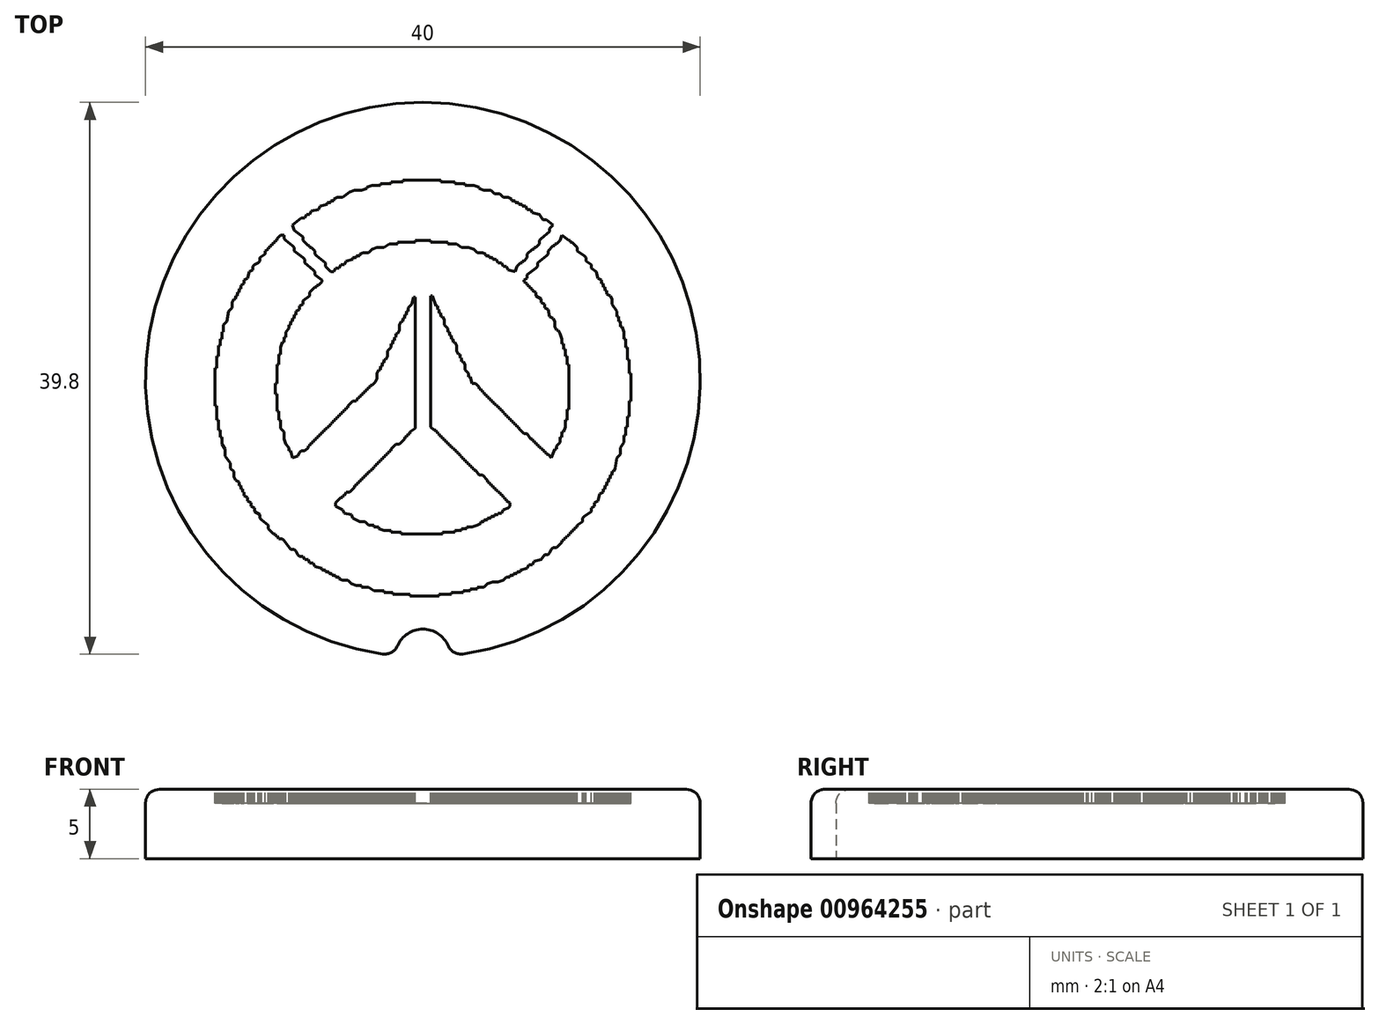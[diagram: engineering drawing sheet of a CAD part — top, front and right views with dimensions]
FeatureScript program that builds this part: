
annotation { "Feature Type Name" : "Feature", "Feature Type Description" : "" }
export const myFeature = defineFeature(function(context is Context, id is Id, definition is map)
    precondition{}
    {
        {
            var Q0;
            Q0=qCreatedBy(makeId("Front.planeOp"),FACE);
            var sketch = newSketch(context, id + "F0", { "sketchPlane" : qUnion([Q0])});
            skLineSegment(sketch, "E0.bottom", {"start": v(0, 0) * mm, "end": v(-20, 0) * mm});
            skLineSegment(sketch, "E0.top", {"start": v(0, 5) * mm, "end": v(-20, 5) * mm});
            skLineSegment(sketch, "E0.left", {"start": v(0, 0) * mm, "end": v(0, 5) * mm});
            skLineSegment(sketch, "E0.right", {"start": v(-20, 0) * mm, "end": v(-20, 5) * mm});
            skSolve(sketch);
        }
        {
            var Q0;
            Q0 = qSketchRegion(id + "F0", true);
            var Q1;
            Q1=sQuery(id+"F0.wireOp",EDGE,"E0.left");
            revolve(context, id + "F1", {"surfaceOperationType" : NewSurfaceOperationType.NEW, "entities" : qUnion([Q0]), "axis" : qUnion([Q1]), "revolveType" : RevolveType.FULL});
        }
        {
            var Q0;
            Q0=qCreatedBy(makeId("Top.planeOp"),FACE);
            var sketch = newSketch(context, id + "F2", { "sketchPlane" : qUnion([Q0])});
            skLineSegment(sketch, "E1", {"start": v(0, 0) * mm, "end": v(0, -20) * mm});
            skCircle(sketch, "E2", {"center": v(0, -20) * mm, "radius": 2 * mm});
            skSolve(sketch);
        }
        {
            var Q0;
            Q0 = qSketchRegion(id + "F2", true);
            extrude(context, id + "F3", {"entities" : qUnion([Q0]), "operationType" : NewBodyOperationType.REMOVE, "depth" : 25 * mm, "offsetDistance" : 25 * mm});
        }
        {
            var Q0;
            Q0=makeQuery(id+"F1.opRevolve","SWEPT_EDGE",EDGE,{"disambiguationData":[OSD([sQuery(id+"F0.wireOp",EDGE,"E0.top"),sQuery(id+"F0.wireOp",EDGE,"E0.right")])]});
            fillet(context, id + "F4", {"entities" : qUnion([Q0]), "radius" : 1 * mm, "tangentPropagation" : true, "allowEdgeOverflow" : false});
        }
        {
            var Q0;
            Q0=makeQuery(id+"F3.boolean.opBoolean","INTERSECT",EDGE,{"derivedFrom":[makeQuery(id+"F1.opRevolve","SWEPT_FACE",FACE,{"disambiguationData":[OSD([sQuery(id+"F0.wireOp",EDGE,"E0.top")])]}),makeQuery(id+"F3.opExtrude","SWEPT_FACE",FACE,{"disambiguationData":[OSD([sQuery(id+"F2.wireOp",EDGE,"E2")])]})]});
            fillet(context, id + "F5", {"entities" : qUnion([Q0]), "radius" : 1 * mm, "tangentPropagation" : true, "allowEdgeOverflow" : false});
        }
        {
            var Q0;
            Q0=qCreatedBy(makeId("Top.planeOp"),FACE);
            cPlane(context, id + "F6", {"entities" : qUnion([Q0]), "cplaneType" : CPlaneType.OFFSET, "offset" : 5 * mm, "width" : 150 * mm, "height" : 150 * mm});
        }
        {
            var Q0;
            Q0=qCreatedBy(id+"F6.planeOp",FACE);
            var sketch = newSketch(context, id + "F7", { "sketchPlane" : qUnion([Q0])});
            skLineSegment(sketch, "E3", {"start": v(-1.43, 14.4) * mm, "end": v(-1.43, 14.28) * mm});
            skLineSegment(sketch, "E4", {"start": v(-1.43, 14.28) * mm, "end": v(-2.3, 14.28) * mm});
            skLineSegment(sketch, "E5", {"start": v(-2.3, 14.28) * mm, "end": v(-2.3, 14.15) * mm});
            skLineSegment(sketch, "E6", {"start": v(-2.3, 14.15) * mm, "end": v(-3.05, 14.15) * mm});
            skLineSegment(sketch, "E7", {"start": v(-3.05, 14.15) * mm, "end": v(-3.05, 14.03) * mm});
            skLineSegment(sketch, "E8", {"start": v(-3.05, 14.03) * mm, "end": v(-3.67, 14.03) * mm});
            skLineSegment(sketch, "E9", {"start": v(-3.67, 14.03) * mm, "end": v(-4.05, 13.9) * mm});
            skLineSegment(sketch, "E10", {"start": v(-4.05, 13.9) * mm, "end": v(-4.05, 13.78) * mm});
            skLineSegment(sketch, "E11", {"start": v(-4.05, 13.78) * mm, "end": v(-4.42, 13.65) * mm});
            skLineSegment(sketch, "E12", {"start": v(-4.42, 13.65) * mm, "end": v(-4.92, 13.65) * mm});
            skLineSegment(sketch, "E13", {"start": v(-4.92, 13.65) * mm, "end": v(-5.3, 13.53) * mm});
            skLineSegment(sketch, "E14", {"start": v(-5.3, 13.53) * mm, "end": v(-5.79, 13.16) * mm});
            skLineSegment(sketch, "E15", {"start": v(-5.79, 13.16) * mm, "end": v(-6.16, 13.16) * mm});
            skLineSegment(sketch, "E16", {"start": v(-6.16, 13.16) * mm, "end": v(-6.41, 13.03) * mm});
            skLineSegment(sketch, "E17", {"start": v(-6.41, 13.03) * mm, "end": v(-6.41, 12.9) * mm});
            skLineSegment(sketch, "E18", {"start": v(-6.41, 12.9) * mm, "end": v(-6.66, 12.9) * mm});
            skLineSegment(sketch, "E19", {"start": v(-6.66, 12.9) * mm, "end": v(-6.66, 12.78) * mm});
            skLineSegment(sketch, "E20", {"start": v(-6.66, 12.78) * mm, "end": v(-6.9, 12.78) * mm});
            skLineSegment(sketch, "E21", {"start": v(-6.9, 12.78) * mm, "end": v(-6.9, 12.66) * mm});
            skLineSegment(sketch, "E22", {"start": v(-6.9, 12.66) * mm, "end": v(-7.4, 12.53) * mm});
            skLineSegment(sketch, "E23", {"start": v(-7.4, 12.53) * mm, "end": v(-7.53, 12.28) * mm});
            skLineSegment(sketch, "E24", {"start": v(-7.53, 12.28) * mm, "end": v(-8.03, 12.16) * mm});
            skLineSegment(sketch, "E25", {"start": v(-8.03, 12.16) * mm, "end": v(-8.15, 11.91) * mm});
            skLineSegment(sketch, "E26", {"start": v(-8.15, 11.91) * mm, "end": v(-8.4, 11.91) * mm});
            skLineSegment(sketch, "E27", {"start": v(-8.4, 11.91) * mm, "end": v(-8.53, 11.66) * mm});
            skLineSegment(sketch, "E28", {"start": v(-8.53, 11.66) * mm, "end": v(-8.78, 11.66) * mm});
            skLineSegment(sketch, "E29", {"start": v(-8.78, 11.66) * mm, "end": v(-9.4, 11.16) * mm});
            skLineSegment(sketch, "E30", {"start": v(-9.4, 11.16) * mm, "end": v(-9.27, 10.8) * mm});
            skLineSegment(sketch, "E31", {"start": v(-9.27, 10.8) * mm, "end": v(-8.65, 10.3) * mm});
            skLineSegment(sketch, "E32", {"start": v(-8.65, 10.3) * mm, "end": v(-8.65, 10.04) * mm});
            skLineSegment(sketch, "E33", {"start": v(-8.65, 10.04) * mm, "end": v(-8.53, 9.92) * mm});
            skLineSegment(sketch, "E34", {"start": v(-8.53, 9.92) * mm, "end": v(-8.28, 9.67) * mm});
            skLineSegment(sketch, "E35", {"start": v(-8.28, 9.67) * mm, "end": v(-8.15, 9.67) * mm});
            skLineSegment(sketch, "E36", {"start": v(-8.15, 9.67) * mm, "end": v(-8.15, 9.55) * mm});
            skLineSegment(sketch, "E37", {"start": v(-8.15, 9.55) * mm, "end": v(-8.03, 9.55) * mm});
            skLineSegment(sketch, "E38", {"start": v(-8.03, 9.55) * mm, "end": v(-7.78, 9.3) * mm});
            skLineSegment(sketch, "E39", {"start": v(-7.78, 9.3) * mm, "end": v(-7.78, 9.05) * mm});
            skLineSegment(sketch, "E40", {"start": v(-7.78, 9.05) * mm, "end": v(-7.66, 8.92) * mm});
            skLineSegment(sketch, "E41", {"start": v(-7.66, 8.92) * mm, "end": v(-7.03, 8.42) * mm});
            skLineSegment(sketch, "E42", {"start": v(-7.03, 8.42) * mm, "end": v(-7.03, 8.18) * mm});
            skLineSegment(sketch, "E43", {"start": v(-7.03, 8.18) * mm, "end": v(-6.9, 8.05) * mm});
            skLineSegment(sketch, "E44", {"start": v(-6.9, 8.05) * mm, "end": v(-6.78, 7.93) * mm});
            skLineSegment(sketch, "E45", {"start": v(-6.78, 7.93) * mm, "end": v(-6.66, 7.8) * mm});
            skLineSegment(sketch, "E46", {"start": v(-6.66, 7.8) * mm, "end": v(-6.41, 7.8) * mm});
            skLineSegment(sketch, "E47", {"start": v(-6.41, 7.8) * mm, "end": v(-6.29, 8.05) * mm});
            skLineSegment(sketch, "E48", {"start": v(-6.29, 8.05) * mm, "end": v(-6.04, 8.05) * mm});
            skLineSegment(sketch, "E49", {"start": v(-6.04, 8.05) * mm, "end": v(-5.91, 8.3) * mm});
            skLineSegment(sketch, "E50", {"start": v(-5.91, 8.3) * mm, "end": v(-5.66, 8.3) * mm});
            skLineSegment(sketch, "E51", {"start": v(-5.66, 8.3) * mm, "end": v(-5.54, 8.55) * mm});
            skLineSegment(sketch, "E52", {"start": v(-5.54, 8.55) * mm, "end": v(-5.04, 8.67) * mm});
            skLineSegment(sketch, "E53", {"start": v(-5.04, 8.67) * mm, "end": v(-5.04, 8.8) * mm});
            skLineSegment(sketch, "E54", {"start": v(-5.04, 8.8) * mm, "end": v(-4.8, 8.8) * mm});
            skLineSegment(sketch, "E55", {"start": v(-4.8, 8.8) * mm, "end": v(-4.8, 8.92) * mm});
            skLineSegment(sketch, "E56", {"start": v(-4.8, 8.92) * mm, "end": v(-4.54, 8.92) * mm});
            skLineSegment(sketch, "E57", {"start": v(-4.54, 8.92) * mm, "end": v(-4.54, 9.05) * mm});
            skLineSegment(sketch, "E58", {"start": v(-4.54, 9.05) * mm, "end": v(-4.3, 9.17) * mm});
            skLineSegment(sketch, "E59", {"start": v(-4.3, 9.17) * mm, "end": v(-3.92, 9.17) * mm});
            skLineSegment(sketch, "E60", {"start": v(-3.92, 9.17) * mm, "end": v(-3.67, 9.42) * mm});
            skLineSegment(sketch, "E61", {"start": v(-3.67, 9.42) * mm, "end": v(-3.3, 9.55) * mm});
            skLineSegment(sketch, "E62", {"start": v(-3.3, 9.55) * mm, "end": v(-2.8, 9.55) * mm});
            skLineSegment(sketch, "E63", {"start": v(-2.8, 9.55) * mm, "end": v(-2.43, 9.8) * mm});
            skLineSegment(sketch, "E64", {"start": v(-2.43, 9.8) * mm, "end": v(-1.8, 9.8) * mm});
            skLineSegment(sketch, "E65", {"start": v(-1.8, 9.8) * mm, "end": v(-1.8, 9.92) * mm});
            skLineSegment(sketch, "E66", {"start": v(-1.8, 9.92) * mm, "end": v(-1.43, 9.92) * mm});
            skLineSegment(sketch, "E67", {"start": v(-1.43, 9.92) * mm, "end": v(-0.56, 9.92) * mm});
            skLineSegment(sketch, "E68", {"start": v(-0.56, 9.92) * mm, "end": v(-0.56, 10.04) * mm});
            skLineSegment(sketch, "E69", {"start": v(-0.56, 10.04) * mm, "end": v(-0.19, 10.04) * mm});
            skLineSegment(sketch, "E70", {"start": v(-0.19, 10.04) * mm, "end": v(0.19, 10.04) * mm});
            skLineSegment(sketch, "E71", {"start": v(0.19, 10.04) * mm, "end": v(0.56, 10.04) * mm});
            skLineSegment(sketch, "E72", {"start": v(0.56, 10.04) * mm, "end": v(0.56, 9.92) * mm});
            skLineSegment(sketch, "E73", {"start": v(0.56, 9.92) * mm, "end": v(0.93, 9.92) * mm});
            skLineSegment(sketch, "E74", {"start": v(0.93, 9.92) * mm, "end": v(1.8, 9.92) * mm});
            skLineSegment(sketch, "E75", {"start": v(1.8, 9.92) * mm, "end": v(1.8, 9.8) * mm});
            skLineSegment(sketch, "E76", {"start": v(1.8, 9.8) * mm, "end": v(2.43, 9.8) * mm});
            skLineSegment(sketch, "E77", {"start": v(2.43, 9.8) * mm, "end": v(2.8, 9.55) * mm});
            skLineSegment(sketch, "E78", {"start": v(2.8, 9.55) * mm, "end": v(3.3, 9.55) * mm});
            skLineSegment(sketch, "E79", {"start": v(3.3, 9.55) * mm, "end": v(3.67, 9.42) * mm});
            skLineSegment(sketch, "E80", {"start": v(3.67, 9.42) * mm, "end": v(3.92, 9.17) * mm});
            skLineSegment(sketch, "E81", {"start": v(3.92, 9.17) * mm, "end": v(4.3, 9.17) * mm});
            skLineSegment(sketch, "E82", {"start": v(4.3, 9.17) * mm, "end": v(4.54, 9.05) * mm});
            skLineSegment(sketch, "E83", {"start": v(4.54, 9.05) * mm, "end": v(4.54, 8.92) * mm});
            skLineSegment(sketch, "E84", {"start": v(4.54, 8.92) * mm, "end": v(4.8, 8.92) * mm});
            skLineSegment(sketch, "E85", {"start": v(4.8, 8.92) * mm, "end": v(4.8, 8.8) * mm});
            skLineSegment(sketch, "E86", {"start": v(4.8, 8.8) * mm, "end": v(5.04, 8.8) * mm});
            skLineSegment(sketch, "E87", {"start": v(5.04, 8.8) * mm, "end": v(5.04, 8.67) * mm});
            skLineSegment(sketch, "E88", {"start": v(5.04, 8.67) * mm, "end": v(5.3, 8.67) * mm});
            skLineSegment(sketch, "E89", {"start": v(5.3, 8.67) * mm, "end": v(5.41, 8.42) * mm});
            skLineSegment(sketch, "E90", {"start": v(5.41, 8.42) * mm, "end": v(5.66, 8.42) * mm});
            skLineSegment(sketch, "E91", {"start": v(5.66, 8.42) * mm, "end": v(5.79, 8.18) * mm});
            skLineSegment(sketch, "E92", {"start": v(5.79, 8.18) * mm, "end": v(6.04, 8.18) * mm});
            skLineSegment(sketch, "E93", {"start": v(6.04, 8.18) * mm, "end": v(6.16, 7.93) * mm});
            skLineSegment(sketch, "E94", {"start": v(6.16, 7.93) * mm, "end": v(6.66, 7.8) * mm});
            skLineSegment(sketch, "E95", {"start": v(6.66, 7.8) * mm, "end": v(6.78, 8.18) * mm});
            skLineSegment(sketch, "E96", {"start": v(6.78, 8.18) * mm, "end": v(7.03, 8.42) * mm});
            skLineSegment(sketch, "E97", {"start": v(7.03, 8.42) * mm, "end": v(7.16, 8.42) * mm});
            skLineSegment(sketch, "E98", {"start": v(7.16, 8.42) * mm, "end": v(7.16, 8.55) * mm});
            skLineSegment(sketch, "E99", {"start": v(7.16, 8.55) * mm, "end": v(7.28, 8.55) * mm});
            skLineSegment(sketch, "E100", {"start": v(7.28, 8.55) * mm, "end": v(7.53, 8.8) * mm});
            skLineSegment(sketch, "E101", {"start": v(7.53, 8.8) * mm, "end": v(7.53, 9.05) * mm});
            skLineSegment(sketch, "E102", {"start": v(7.53, 9.05) * mm, "end": v(7.66, 9.17) * mm});
            skLineSegment(sketch, "E103", {"start": v(7.66, 9.17) * mm, "end": v(7.9, 9.42) * mm});
            skLineSegment(sketch, "E104", {"start": v(7.9, 9.42) * mm, "end": v(8.03, 9.42) * mm});
            skLineSegment(sketch, "E105", {"start": v(8.03, 9.42) * mm, "end": v(8.03, 9.55) * mm});
            skLineSegment(sketch, "E106", {"start": v(8.03, 9.55) * mm, "end": v(8.15, 9.55) * mm});
            skLineSegment(sketch, "E107", {"start": v(8.15, 9.55) * mm, "end": v(8.4, 9.8) * mm});
            skLineSegment(sketch, "E108", {"start": v(8.4, 9.8) * mm, "end": v(8.4, 10.04) * mm});
            skLineSegment(sketch, "E109", {"start": v(8.4, 10.04) * mm, "end": v(8.53, 10.17) * mm});
            skLineSegment(sketch, "E110", {"start": v(8.53, 10.17) * mm, "end": v(9.15, 10.67) * mm});
            skLineSegment(sketch, "E111", {"start": v(9.15, 10.67) * mm, "end": v(9.15, 10.91) * mm});
            skLineSegment(sketch, "E112", {"start": v(9.15, 10.91) * mm, "end": v(9.4, 11.16) * mm});
            skLineSegment(sketch, "E113", {"start": v(9.4, 11.16) * mm, "end": v(8.9, 11.54) * mm});
            skLineSegment(sketch, "E114", {"start": v(8.9, 11.54) * mm, "end": v(8.65, 11.54) * mm});
            skLineSegment(sketch, "E115", {"start": v(8.65, 11.54) * mm, "end": v(8.4, 11.91) * mm});
            skLineSegment(sketch, "E116", {"start": v(8.4, 11.91) * mm, "end": v(7.9, 12.03) * mm});
            skLineSegment(sketch, "E117", {"start": v(7.9, 12.03) * mm, "end": v(7.78, 12.28) * mm});
            skLineSegment(sketch, "E118", {"start": v(7.78, 12.28) * mm, "end": v(7.53, 12.28) * mm});
            skLineSegment(sketch, "E119", {"start": v(7.53, 12.28) * mm, "end": v(7.4, 12.53) * mm});
            skLineSegment(sketch, "E120", {"start": v(7.4, 12.53) * mm, "end": v(7.16, 12.53) * mm});
            skLineSegment(sketch, "E121", {"start": v(7.16, 12.53) * mm, "end": v(7.16, 12.66) * mm});
            skLineSegment(sketch, "E122", {"start": v(7.16, 12.66) * mm, "end": v(6.9, 12.66) * mm});
            skLineSegment(sketch, "E123", {"start": v(6.9, 12.66) * mm, "end": v(6.9, 12.78) * mm});
            skLineSegment(sketch, "E124", {"start": v(6.9, 12.78) * mm, "end": v(6.66, 12.78) * mm});
            skLineSegment(sketch, "E125", {"start": v(6.66, 12.78) * mm, "end": v(6.66, 12.9) * mm});
            skLineSegment(sketch, "E126", {"start": v(6.66, 12.9) * mm, "end": v(6.41, 12.9) * mm});
            skLineSegment(sketch, "E127", {"start": v(6.41, 12.9) * mm, "end": v(6.41, 13.03) * mm});
            skLineSegment(sketch, "E128", {"start": v(6.41, 13.03) * mm, "end": v(6.16, 13.16) * mm});
            skLineSegment(sketch, "E129", {"start": v(6.16, 13.16) * mm, "end": v(5.79, 13.16) * mm});
            skLineSegment(sketch, "E130", {"start": v(5.79, 13.16) * mm, "end": v(5.54, 13.4) * mm});
            skLineSegment(sketch, "E131", {"start": v(5.54, 13.4) * mm, "end": v(5.17, 13.4) * mm});
            skLineSegment(sketch, "E132", {"start": v(5.17, 13.4) * mm, "end": v(4.92, 13.65) * mm});
            skLineSegment(sketch, "E133", {"start": v(4.92, 13.65) * mm, "end": v(4.42, 13.65) * mm});
            skLineSegment(sketch, "E134", {"start": v(4.42, 13.65) * mm, "end": v(4.05, 13.78) * mm});
            skLineSegment(sketch, "E135", {"start": v(4.05, 13.78) * mm, "end": v(4.05, 13.9) * mm});
            skLineSegment(sketch, "E136", {"start": v(4.05, 13.9) * mm, "end": v(3.67, 14.03) * mm});
            skLineSegment(sketch, "E137", {"start": v(3.67, 14.03) * mm, "end": v(3.05, 14.03) * mm});
            skLineSegment(sketch, "E138", {"start": v(3.05, 14.03) * mm, "end": v(3.05, 14.15) * mm});
            skLineSegment(sketch, "E139", {"start": v(3.05, 14.15) * mm, "end": v(2.3, 14.15) * mm});
            skLineSegment(sketch, "E140", {"start": v(2.3, 14.15) * mm, "end": v(2.3, 14.28) * mm});
            skLineSegment(sketch, "E141", {"start": v(2.3, 14.28) * mm, "end": v(1.3, 14.28) * mm});
            skLineSegment(sketch, "E142", {"start": v(1.3, 14.28) * mm, "end": v(1.3, 14.4) * mm});
            skLineSegment(sketch, "E143", {"start": v(1.3, 14.4) * mm, "end": v(0.93, 14.4) * mm});
            skLineSegment(sketch, "E144", {"start": v(0.93, 14.4) * mm, "end": v(0.44, 14.4) * mm});
            skLineSegment(sketch, "E145", {"start": v(0.44, 14.4) * mm, "end": v(0.31, 14.4) * mm});
            skLineSegment(sketch, "E146", {"start": v(0.31, 14.4) * mm, "end": v(0.19, 14.4) * mm});
            skLineSegment(sketch, "E147", {"start": v(0.19, 14.4) * mm, "end": v(0.06, 14.4) * mm});
            skLineSegment(sketch, "E148", {"start": v(0.06, 14.4) * mm, "end": v(-0.06, 14.4) * mm});
            skLineSegment(sketch, "E149", {"start": v(-0.06, 14.4) * mm, "end": v(-0.19, 14.4) * mm});
            skLineSegment(sketch, "E150", {"start": v(-0.19, 14.4) * mm, "end": v(-0.31, 14.4) * mm});
            skLineSegment(sketch, "E151", {"start": v(-0.31, 14.4) * mm, "end": v(-0.44, 14.4) * mm});
            skLineSegment(sketch, "E152", {"start": v(-0.44, 14.4) * mm, "end": v(-0.56, 14.4) * mm});
            skLineSegment(sketch, "E153", {"start": v(-0.56, 14.4) * mm, "end": v(-0.68, 14.4) * mm});
            skLineSegment(sketch, "E154", {"start": v(-0.68, 14.4) * mm, "end": v(-0.8, 14.4) * mm});
            skLineSegment(sketch, "E155", {"start": v(-0.8, 14.4) * mm, "end": v(-0.93, 14.4) * mm});
            skLineSegment(sketch, "E156", {"start": v(-0.93, 14.4) * mm, "end": v(-1.43, 14.4) * mm});
            skLineSegment(sketch, "E157", {"start": v(-10.27, 10.42) * mm, "end": v(-10.52, 10.17) * mm});
            skLineSegment(sketch, "E158", {"start": v(-10.52, 10.17) * mm, "end": v(-10.52, 10.04) * mm});
            skLineSegment(sketch, "E159", {"start": v(-10.52, 10.04) * mm, "end": v(-10.64, 10.04) * mm});
            skLineSegment(sketch, "E160", {"start": v(-10.64, 10.04) * mm, "end": v(-10.64, 9.92) * mm});
            skLineSegment(sketch, "E161", {"start": v(-10.64, 9.92) * mm, "end": v(-10.77, 9.92) * mm});
            skLineSegment(sketch, "E162", {"start": v(-10.77, 9.92) * mm, "end": v(-10.77, 9.8) * mm});
            skLineSegment(sketch, "E163", {"start": v(-10.77, 9.8) * mm, "end": v(-10.9, 9.8) * mm});
            skLineSegment(sketch, "E164", {"start": v(-10.9, 9.8) * mm, "end": v(-10.9, 9.67) * mm});
            skLineSegment(sketch, "E165", {"start": v(-10.9, 9.67) * mm, "end": v(-11.02, 9.67) * mm});
            skLineSegment(sketch, "E166", {"start": v(-11.02, 9.67) * mm, "end": v(-11.02, 9.55) * mm});
            skLineSegment(sketch, "E167", {"start": v(-11.02, 9.55) * mm, "end": v(-11.14, 9.55) * mm});
            skLineSegment(sketch, "E168", {"start": v(-11.14, 9.55) * mm, "end": v(-11.14, 9.42) * mm});
            skLineSegment(sketch, "E169", {"start": v(-11.14, 9.42) * mm, "end": v(-11.4, 9.3) * mm});
            skLineSegment(sketch, "E170", {"start": v(-11.4, 9.3) * mm, "end": v(-11.4, 9.05) * mm});
            skLineSegment(sketch, "E171", {"start": v(-11.4, 9.05) * mm, "end": v(-11.76, 8.8) * mm});
            skLineSegment(sketch, "E172", {"start": v(-11.76, 8.8) * mm, "end": v(-11.76, 8.55) * mm});
            skLineSegment(sketch, "E173", {"start": v(-11.76, 8.55) * mm, "end": v(-11.89, 8.42) * mm});
            skLineSegment(sketch, "E174", {"start": v(-11.89, 8.42) * mm, "end": v(-12.14, 8.3) * mm});
            skLineSegment(sketch, "E175", {"start": v(-12.14, 8.3) * mm, "end": v(-12.26, 8.18) * mm});
            skLineSegment(sketch, "E176", {"start": v(-12.26, 8.18) * mm, "end": v(-12.26, 7.93) * mm});
            skLineSegment(sketch, "E177", {"start": v(-12.26, 7.93) * mm, "end": v(-12.51, 7.8) * mm});
            skLineSegment(sketch, "E178", {"start": v(-12.51, 7.8) * mm, "end": v(-12.63, 7.3) * mm});
            skLineSegment(sketch, "E179", {"start": v(-12.63, 7.3) * mm, "end": v(-12.88, 7.18) * mm});
            skLineSegment(sketch, "E180", {"start": v(-12.88, 7.18) * mm, "end": v(-12.88, 6.93) * mm});
            skLineSegment(sketch, "E181", {"start": v(-12.88, 6.93) * mm, "end": v(-13.13, 6.8) * mm});
            skLineSegment(sketch, "E182", {"start": v(-13.13, 6.8) * mm, "end": v(-13.13, 6.56) * mm});
            skLineSegment(sketch, "E183", {"start": v(-13.13, 6.56) * mm, "end": v(-13.26, 6.56) * mm});
            skLineSegment(sketch, "E184", {"start": v(-13.26, 6.56) * mm, "end": v(-13.26, 6.3) * mm});
            skLineSegment(sketch, "E185", {"start": v(-13.26, 6.3) * mm, "end": v(-13.38, 6.3) * mm});
            skLineSegment(sketch, "E186", {"start": v(-13.38, 6.3) * mm, "end": v(-13.38, 6.06) * mm});
            skLineSegment(sketch, "E187", {"start": v(-13.38, 6.06) * mm, "end": v(-13.5, 6.06) * mm});
            skLineSegment(sketch, "E188", {"start": v(-13.5, 6.06) * mm, "end": v(-13.5, 5.81) * mm});
            skLineSegment(sketch, "E189", {"start": v(-13.5, 5.81) * mm, "end": v(-13.63, 5.81) * mm});
            skLineSegment(sketch, "E190", {"start": v(-13.63, 5.81) * mm, "end": v(-13.76, 5.56) * mm});
            skLineSegment(sketch, "E191", {"start": v(-13.76, 5.56) * mm, "end": v(-13.76, 5.19) * mm});
            skLineSegment(sketch, "E192", {"start": v(-13.76, 5.19) * mm, "end": v(-14, 4.94) * mm});
            skLineSegment(sketch, "E193", {"start": v(-14, 4.94) * mm, "end": v(-14.13, 4.2) * mm});
            skLineSegment(sketch, "E194", {"start": v(-14.13, 4.2) * mm, "end": v(-14.38, 3.94) * mm});
            skLineSegment(sketch, "E195", {"start": v(-14.38, 3.94) * mm, "end": v(-14.38, 3.45) * mm});
            skLineSegment(sketch, "E196", {"start": v(-14.38, 3.45) * mm, "end": v(-14.5, 3.45) * mm});
            skLineSegment(sketch, "E197", {"start": v(-14.5, 3.45) * mm, "end": v(-14.5, 2.95) * mm});
            skLineSegment(sketch, "E198", {"start": v(-14.5, 2.95) * mm, "end": v(-14.63, 2.95) * mm});
            skLineSegment(sketch, "E199", {"start": v(-14.63, 2.95) * mm, "end": v(-14.63, 2.45) * mm});
            skLineSegment(sketch, "E200", {"start": v(-14.63, 2.45) * mm, "end": v(-14.75, 2.45) * mm});
            skLineSegment(sketch, "E201", {"start": v(-14.75, 2.45) * mm, "end": v(-14.75, 1.7) * mm});
            skLineSegment(sketch, "E202", {"start": v(-14.75, 1.7) * mm, "end": v(-14.88, 1.7) * mm});
            skLineSegment(sketch, "E203", {"start": v(-14.88, 1.7) * mm, "end": v(-14.88, 0.83) * mm});
            skLineSegment(sketch, "E204", {"start": v(-14.88, 0.83) * mm, "end": v(-15, 0.83) * mm});
            skLineSegment(sketch, "E205", {"start": v(-15, 0.83) * mm, "end": v(-15, 0.46) * mm});
            skLineSegment(sketch, "E206", {"start": v(-15, 0.46) * mm, "end": v(-15, -0.04) * mm});
            skLineSegment(sketch, "E207", {"start": v(-15, -0.04) * mm, "end": v(-15, -0.16) * mm});
            skLineSegment(sketch, "E208", {"start": v(-15, -0.16) * mm, "end": v(-15, -0.29) * mm});
            skLineSegment(sketch, "E209", {"start": v(-15, -0.29) * mm, "end": v(-15, -0.41) * mm});
            skLineSegment(sketch, "E210", {"start": v(-15, -0.41) * mm, "end": v(-15, -0.54) * mm});
            skLineSegment(sketch, "E211", {"start": v(-15, -0.54) * mm, "end": v(-15, -0.66) * mm});
            skLineSegment(sketch, "E212", {"start": v(-15, -0.66) * mm, "end": v(-15, -0.79) * mm});
            skLineSegment(sketch, "E213", {"start": v(-15, -0.79) * mm, "end": v(-15, -0.91) * mm});
            skLineSegment(sketch, "E214", {"start": v(-15, -0.91) * mm, "end": v(-15, -1.04) * mm});
            skLineSegment(sketch, "E215", {"start": v(-15, -1.04) * mm, "end": v(-15, -1.16) * mm});
            skLineSegment(sketch, "E216", {"start": v(-15, -1.16) * mm, "end": v(-15, -1.28) * mm});
            skLineSegment(sketch, "E217", {"start": v(-15, -1.28) * mm, "end": v(-15, -1.4) * mm});
            skLineSegment(sketch, "E218", {"start": v(-15, -1.4) * mm, "end": v(-15, -1.9) * mm});
            skLineSegment(sketch, "E219", {"start": v(-15, -1.9) * mm, "end": v(-14.88, -1.9) * mm});
            skLineSegment(sketch, "E220", {"start": v(-14.88, -1.9) * mm, "end": v(-14.88, -2.9) * mm});
            skLineSegment(sketch, "E221", {"start": v(-14.88, -2.9) * mm, "end": v(-14.75, -2.9) * mm});
            skLineSegment(sketch, "E222", {"start": v(-14.75, -2.9) * mm, "end": v(-14.75, -3.65) * mm});
            skLineSegment(sketch, "E223", {"start": v(-14.75, -3.65) * mm, "end": v(-14.63, -3.65) * mm});
            skLineSegment(sketch, "E224", {"start": v(-14.63, -3.65) * mm, "end": v(-14.63, -4.15) * mm});
            skLineSegment(sketch, "E225", {"start": v(-14.63, -4.15) * mm, "end": v(-14.5, -4.15) * mm});
            skLineSegment(sketch, "E226", {"start": v(-14.5, -4.15) * mm, "end": v(-14.5, -4.65) * mm});
            skLineSegment(sketch, "E227", {"start": v(-14.5, -4.65) * mm, "end": v(-14.25, -5.02) * mm});
            skLineSegment(sketch, "E228", {"start": v(-14.25, -5.02) * mm, "end": v(-14.25, -5.52) * mm});
            skLineSegment(sketch, "E229", {"start": v(-14.25, -5.52) * mm, "end": v(-13.88, -6.01) * mm});
            skLineSegment(sketch, "E230", {"start": v(-13.88, -6.01) * mm, "end": v(-13.88, -6.39) * mm});
            skLineSegment(sketch, "E231", {"start": v(-13.88, -6.39) * mm, "end": v(-13.63, -6.64) * mm});
            skLineSegment(sketch, "E232", {"start": v(-13.63, -6.64) * mm, "end": v(-13.63, -7.01) * mm});
            skLineSegment(sketch, "E233", {"start": v(-13.63, -7.01) * mm, "end": v(-13.5, -7.26) * mm});
            skLineSegment(sketch, "E234", {"start": v(-13.5, -7.26) * mm, "end": v(-13.26, -7.38) * mm});
            skLineSegment(sketch, "E235", {"start": v(-13.26, -7.38) * mm, "end": v(-13.26, -7.63) * mm});
            skLineSegment(sketch, "E236", {"start": v(-13.26, -7.63) * mm, "end": v(-13.13, -7.63) * mm});
            skLineSegment(sketch, "E237", {"start": v(-13.13, -7.63) * mm, "end": v(-13.13, -7.88) * mm});
            skLineSegment(sketch, "E238", {"start": v(-13.13, -7.88) * mm, "end": v(-13, -7.88) * mm});
            skLineSegment(sketch, "E239", {"start": v(-13, -7.88) * mm, "end": v(-13, -8.13) * mm});
            skLineSegment(sketch, "E240", {"start": v(-13, -8.13) * mm, "end": v(-12.88, -8.13) * mm});
            skLineSegment(sketch, "E241", {"start": v(-12.88, -8.13) * mm, "end": v(-12.88, -8.38) * mm});
            skLineSegment(sketch, "E242", {"start": v(-12.88, -8.38) * mm, "end": v(-12.63, -8.5) * mm});
            skLineSegment(sketch, "E243", {"start": v(-12.63, -8.5) * mm, "end": v(-12.63, -8.75) * mm});
            skLineSegment(sketch, "E244", {"start": v(-12.63, -8.75) * mm, "end": v(-12.39, -8.88) * mm});
            skLineSegment(sketch, "E245", {"start": v(-12.39, -8.88) * mm, "end": v(-12.39, -9.13) * mm});
            skLineSegment(sketch, "E246", {"start": v(-12.39, -9.13) * mm, "end": v(-12.14, -9.25) * mm});
            skLineSegment(sketch, "E247", {"start": v(-12.14, -9.25) * mm, "end": v(-12.14, -9.5) * mm});
            skLineSegment(sketch, "E248", {"start": v(-12.14, -9.5) * mm, "end": v(-11.76, -9.75) * mm});
            skLineSegment(sketch, "E249", {"start": v(-11.76, -9.75) * mm, "end": v(-11.76, -10) * mm});
            skLineSegment(sketch, "E250", {"start": v(-11.76, -10) * mm, "end": v(-11.64, -10.12) * mm});
            skLineSegment(sketch, "E251", {"start": v(-11.64, -10.12) * mm, "end": v(-11.14, -10.5) * mm});
            skLineSegment(sketch, "E252", {"start": v(-11.14, -10.5) * mm, "end": v(-11.14, -10.75) * mm});
            skLineSegment(sketch, "E253", {"start": v(-11.14, -10.75) * mm, "end": v(-11.02, -10.87) * mm});
            skLineSegment(sketch, "E254", {"start": v(-11.02, -10.87) * mm, "end": v(-10.77, -11.12) * mm});
            skLineSegment(sketch, "E255", {"start": v(-10.77, -11.12) * mm, "end": v(-10.64, -11.12) * mm});
            skLineSegment(sketch, "E256", {"start": v(-10.64, -11.12) * mm, "end": v(-10.64, -11.24) * mm});
            skLineSegment(sketch, "E257", {"start": v(-10.64, -11.24) * mm, "end": v(-10.52, -11.24) * mm});
            skLineSegment(sketch, "E258", {"start": v(-10.52, -11.24) * mm, "end": v(-10.4, -11.5) * mm});
            skLineSegment(sketch, "E259", {"start": v(-10.4, -11.5) * mm, "end": v(-10.15, -11.5) * mm});
            skLineSegment(sketch, "E260", {"start": v(-10.15, -11.5) * mm, "end": v(-10.02, -11.62) * mm});
            skLineSegment(sketch, "E261", {"start": v(-10.02, -11.62) * mm, "end": v(-9.52, -12.24) * mm});
            skLineSegment(sketch, "E262", {"start": v(-9.52, -12.24) * mm, "end": v(-9.27, -12.24) * mm});
            skLineSegment(sketch, "E263", {"start": v(-9.27, -12.24) * mm, "end": v(-9.15, -12.36) * mm});
            skLineSegment(sketch, "E264", {"start": v(-9.15, -12.36) * mm, "end": v(-9.02, -12.61) * mm});
            skLineSegment(sketch, "E265", {"start": v(-9.02, -12.61) * mm, "end": v(-8.9, -12.74) * mm});
            skLineSegment(sketch, "E266", {"start": v(-8.9, -12.74) * mm, "end": v(-8.65, -12.74) * mm});
            skLineSegment(sketch, "E267", {"start": v(-8.65, -12.74) * mm, "end": v(-8.53, -12.99) * mm});
            skLineSegment(sketch, "E268", {"start": v(-8.53, -12.99) * mm, "end": v(-8.28, -12.99) * mm});
            skLineSegment(sketch, "E269", {"start": v(-8.28, -12.99) * mm, "end": v(-8.15, -13.23) * mm});
            skLineSegment(sketch, "E270", {"start": v(-8.15, -13.23) * mm, "end": v(-7.9, -13.23) * mm});
            skLineSegment(sketch, "E271", {"start": v(-7.9, -13.23) * mm, "end": v(-7.78, -13.48) * mm});
            skLineSegment(sketch, "E272", {"start": v(-7.78, -13.48) * mm, "end": v(-7.28, -13.6) * mm});
            skLineSegment(sketch, "E273", {"start": v(-7.28, -13.6) * mm, "end": v(-7.28, -13.73) * mm});
            skLineSegment(sketch, "E274", {"start": v(-7.28, -13.73) * mm, "end": v(-7.03, -13.73) * mm});
            skLineSegment(sketch, "E275", {"start": v(-7.03, -13.73) * mm, "end": v(-7.03, -13.86) * mm});
            skLineSegment(sketch, "E276", {"start": v(-7.03, -13.86) * mm, "end": v(-6.78, -13.86) * mm});
            skLineSegment(sketch, "E277", {"start": v(-6.78, -13.86) * mm, "end": v(-6.78, -13.98) * mm});
            skLineSegment(sketch, "E278", {"start": v(-6.78, -13.98) * mm, "end": v(-6.54, -13.98) * mm});
            skLineSegment(sketch, "E279", {"start": v(-6.54, -13.98) * mm, "end": v(-6.54, -14.1) * mm});
            skLineSegment(sketch, "E280", {"start": v(-6.54, -14.1) * mm, "end": v(-6.29, -14.1) * mm});
            skLineSegment(sketch, "E281", {"start": v(-6.29, -14.1) * mm, "end": v(-6.29, -14.23) * mm});
            skLineSegment(sketch, "E282", {"start": v(-6.29, -14.23) * mm, "end": v(-6.04, -14.23) * mm});
            skLineSegment(sketch, "E283", {"start": v(-6.04, -14.23) * mm, "end": v(-6.04, -14.36) * mm});
            skLineSegment(sketch, "E284", {"start": v(-6.04, -14.36) * mm, "end": v(-5.79, -14.48) * mm});
            skLineSegment(sketch, "E285", {"start": v(-5.79, -14.48) * mm, "end": v(-5.41, -14.48) * mm});
            skLineSegment(sketch, "E286", {"start": v(-5.41, -14.48) * mm, "end": v(-5.17, -14.73) * mm});
            skLineSegment(sketch, "E287", {"start": v(-5.17, -14.73) * mm, "end": v(-4.8, -14.85) * mm});
            skLineSegment(sketch, "E288", {"start": v(-4.8, -14.85) * mm, "end": v(-4.42, -14.85) * mm});
            skLineSegment(sketch, "E289", {"start": v(-4.42, -14.85) * mm, "end": v(-4.42, -14.98) * mm});
            skLineSegment(sketch, "E290", {"start": v(-4.42, -14.98) * mm, "end": v(-3.92, -14.98) * mm});
            skLineSegment(sketch, "E291", {"start": v(-3.92, -14.98) * mm, "end": v(-3.55, -15.23) * mm});
            skLineSegment(sketch, "E292", {"start": v(-3.55, -15.23) * mm, "end": v(-2.8, -15.23) * mm});
            skLineSegment(sketch, "E293", {"start": v(-2.8, -15.23) * mm, "end": v(-2.8, -15.35) * mm});
            skLineSegment(sketch, "E294", {"start": v(-2.8, -15.35) * mm, "end": v(-2.18, -15.35) * mm});
            skLineSegment(sketch, "E295", {"start": v(-2.18, -15.35) * mm, "end": v(-2.18, -15.48) * mm});
            skLineSegment(sketch, "E296", {"start": v(-2.18, -15.48) * mm, "end": v(-1.8, -15.48) * mm});
            skLineSegment(sketch, "E297", {"start": v(-1.8, -15.48) * mm, "end": v(-0.93, -15.48) * mm});
            skLineSegment(sketch, "E298", {"start": v(-0.93, -15.48) * mm, "end": v(-0.93, -15.6) * mm});
            skLineSegment(sketch, "E299", {"start": v(-0.93, -15.6) * mm, "end": v(-0.56, -15.6) * mm});
            skLineSegment(sketch, "E300", {"start": v(-0.56, -15.6) * mm, "end": v(-0.06, -15.6) * mm});
            skLineSegment(sketch, "E301", {"start": v(-0.06, -15.6) * mm, "end": v(0.06, -15.6) * mm});
            skLineSegment(sketch, "E302", {"start": v(0.06, -15.6) * mm, "end": v(0.19, -15.6) * mm});
            skLineSegment(sketch, "E303", {"start": v(0.19, -15.6) * mm, "end": v(0.31, -15.6) * mm});
            skLineSegment(sketch, "E304", {"start": v(0.31, -15.6) * mm, "end": v(1.18, -15.6) * mm});
            skLineSegment(sketch, "E305", {"start": v(1.18, -15.6) * mm, "end": v(1.18, -15.48) * mm});
            skLineSegment(sketch, "E306", {"start": v(1.18, -15.48) * mm, "end": v(2.05, -15.48) * mm});
            skLineSegment(sketch, "E307", {"start": v(2.05, -15.48) * mm, "end": v(2.05, -15.35) * mm});
            skLineSegment(sketch, "E308", {"start": v(2.05, -15.35) * mm, "end": v(2.93, -15.35) * mm});
            skLineSegment(sketch, "E309", {"start": v(2.93, -15.35) * mm, "end": v(2.93, -15.23) * mm});
            skLineSegment(sketch, "E310", {"start": v(2.93, -15.23) * mm, "end": v(3.42, -15.23) * mm});
            skLineSegment(sketch, "E311", {"start": v(3.42, -15.23) * mm, "end": v(3.42, -15.1) * mm});
            skLineSegment(sketch, "E312", {"start": v(3.42, -15.1) * mm, "end": v(3.92, -15.1) * mm});
            skLineSegment(sketch, "E313", {"start": v(3.92, -15.1) * mm, "end": v(3.92, -14.98) * mm});
            skLineSegment(sketch, "E314", {"start": v(3.92, -14.98) * mm, "end": v(4.42, -14.98) * mm});
            skLineSegment(sketch, "E315", {"start": v(4.42, -14.98) * mm, "end": v(4.67, -14.73) * mm});
            skLineSegment(sketch, "E316", {"start": v(4.67, -14.73) * mm, "end": v(5.04, -14.6) * mm});
            skLineSegment(sketch, "E317", {"start": v(5.04, -14.6) * mm, "end": v(5.41, -14.6) * mm});
            skLineSegment(sketch, "E318", {"start": v(5.41, -14.6) * mm, "end": v(5.79, -14.48) * mm});
            skLineSegment(sketch, "E319", {"start": v(5.79, -14.48) * mm, "end": v(6.04, -14.23) * mm});
            skLineSegment(sketch, "E320", {"start": v(6.04, -14.23) * mm, "end": v(6.29, -14.23) * mm});
            skLineSegment(sketch, "E321", {"start": v(6.29, -14.23) * mm, "end": v(6.29, -14.1) * mm});
            skLineSegment(sketch, "E322", {"start": v(6.29, -14.1) * mm, "end": v(6.54, -14.1) * mm});
            skLineSegment(sketch, "E323", {"start": v(6.54, -14.1) * mm, "end": v(6.54, -13.98) * mm});
            skLineSegment(sketch, "E324", {"start": v(6.54, -13.98) * mm, "end": v(6.78, -13.98) * mm});
            skLineSegment(sketch, "E325", {"start": v(6.78, -13.98) * mm, "end": v(6.78, -13.86) * mm});
            skLineSegment(sketch, "E326", {"start": v(6.78, -13.86) * mm, "end": v(7.03, -13.86) * mm});
            skLineSegment(sketch, "E327", {"start": v(7.03, -13.86) * mm, "end": v(7.03, -13.73) * mm});
            skLineSegment(sketch, "E328", {"start": v(7.03, -13.73) * mm, "end": v(7.53, -13.6) * mm});
            skLineSegment(sketch, "E329", {"start": v(7.53, -13.6) * mm, "end": v(7.66, -13.36) * mm});
            skLineSegment(sketch, "E330", {"start": v(7.66, -13.36) * mm, "end": v(7.9, -13.36) * mm});
            skLineSegment(sketch, "E331", {"start": v(7.9, -13.36) * mm, "end": v(8.03, -13.11) * mm});
            skLineSegment(sketch, "E332", {"start": v(8.03, -13.11) * mm, "end": v(8.53, -12.99) * mm});
            skLineSegment(sketch, "E333", {"start": v(8.53, -12.99) * mm, "end": v(8.78, -12.61) * mm});
            skLineSegment(sketch, "E334", {"start": v(8.78, -12.61) * mm, "end": v(9.02, -12.61) * mm});
            skLineSegment(sketch, "E335", {"start": v(9.02, -12.61) * mm, "end": v(9.15, -12.49) * mm});
            skLineSegment(sketch, "E336", {"start": v(9.15, -12.49) * mm, "end": v(9.27, -12.24) * mm});
            skLineSegment(sketch, "E337", {"start": v(9.27, -12.24) * mm, "end": v(9.4, -12.11) * mm});
            skLineSegment(sketch, "E338", {"start": v(9.4, -12.11) * mm, "end": v(9.65, -12.11) * mm});
            skLineSegment(sketch, "E339", {"start": v(9.65, -12.11) * mm, "end": v(9.77, -12) * mm});
            skLineSegment(sketch, "E340", {"start": v(9.77, -12) * mm, "end": v(10.02, -11.74) * mm});
            skLineSegment(sketch, "E341", {"start": v(10.02, -11.74) * mm, "end": v(10.02, -11.62) * mm});
            skLineSegment(sketch, "E342", {"start": v(10.02, -11.62) * mm, "end": v(10.15, -11.62) * mm});
            skLineSegment(sketch, "E343", {"start": v(10.15, -11.62) * mm, "end": v(10.15, -11.5) * mm});
            skLineSegment(sketch, "E344", {"start": v(10.15, -11.5) * mm, "end": v(10.27, -11.5) * mm});
            skLineSegment(sketch, "E345", {"start": v(10.27, -11.5) * mm, "end": v(10.27, -11.37) * mm});
            skLineSegment(sketch, "E346", {"start": v(10.27, -11.37) * mm, "end": v(10.4, -11.37) * mm});
            skLineSegment(sketch, "E347", {"start": v(10.4, -11.37) * mm, "end": v(10.4, -11.24) * mm});
            skLineSegment(sketch, "E348", {"start": v(10.4, -11.24) * mm, "end": v(10.52, -11.24) * mm});
            skLineSegment(sketch, "E349", {"start": v(10.52, -11.24) * mm, "end": v(10.52, -11.12) * mm});
            skLineSegment(sketch, "E350", {"start": v(10.52, -11.12) * mm, "end": v(10.64, -11.12) * mm});
            skLineSegment(sketch, "E351", {"start": v(10.64, -11.12) * mm, "end": v(10.64, -11) * mm});
            skLineSegment(sketch, "E352", {"start": v(10.64, -11) * mm, "end": v(10.77, -11) * mm});
            skLineSegment(sketch, "E353", {"start": v(10.77, -11) * mm, "end": v(10.77, -10.87) * mm});
            skLineSegment(sketch, "E354", {"start": v(10.77, -10.87) * mm, "end": v(10.9, -10.87) * mm});
            skLineSegment(sketch, "E355", {"start": v(10.9, -10.87) * mm, "end": v(10.9, -10.75) * mm});
            skLineSegment(sketch, "E356", {"start": v(10.9, -10.75) * mm, "end": v(11.02, -10.75) * mm});
            skLineSegment(sketch, "E357", {"start": v(11.02, -10.75) * mm, "end": v(11.02, -10.62) * mm});
            skLineSegment(sketch, "E358", {"start": v(11.02, -10.62) * mm, "end": v(11.14, -10.62) * mm});
            skLineSegment(sketch, "E359", {"start": v(11.14, -10.62) * mm, "end": v(11.14, -10.5) * mm});
            skLineSegment(sketch, "E360", {"start": v(11.14, -10.5) * mm, "end": v(11.51, -10.25) * mm});
            skLineSegment(sketch, "E361", {"start": v(11.51, -10.25) * mm, "end": v(11.51, -10) * mm});
            skLineSegment(sketch, "E362", {"start": v(11.51, -10) * mm, "end": v(11.64, -9.87) * mm});
            skLineSegment(sketch, "E363", {"start": v(11.64, -9.87) * mm, "end": v(12.14, -9.5) * mm});
            skLineSegment(sketch, "E364", {"start": v(12.14, -9.5) * mm, "end": v(12.14, -9.25) * mm});
            skLineSegment(sketch, "E365", {"start": v(12.14, -9.25) * mm, "end": v(12.39, -9.13) * mm});
            skLineSegment(sketch, "E366", {"start": v(12.39, -9.13) * mm, "end": v(12.39, -8.88) * mm});
            skLineSegment(sketch, "E367", {"start": v(12.39, -8.88) * mm, "end": v(12.63, -8.75) * mm});
            skLineSegment(sketch, "E368", {"start": v(12.63, -8.75) * mm, "end": v(12.76, -8.26) * mm});
            skLineSegment(sketch, "E369", {"start": v(12.76, -8.26) * mm, "end": v(13, -8.13) * mm});
            skLineSegment(sketch, "E370", {"start": v(13, -8.13) * mm, "end": v(13, -7.88) * mm});
            skLineSegment(sketch, "E371", {"start": v(13, -7.88) * mm, "end": v(13.13, -7.88) * mm});
            skLineSegment(sketch, "E372", {"start": v(13.13, -7.88) * mm, "end": v(13.13, -7.63) * mm});
            skLineSegment(sketch, "E373", {"start": v(13.13, -7.63) * mm, "end": v(13.26, -7.63) * mm});
            skLineSegment(sketch, "E374", {"start": v(13.26, -7.63) * mm, "end": v(13.26, -7.38) * mm});
            skLineSegment(sketch, "E375", {"start": v(13.26, -7.38) * mm, "end": v(13.38, -7.38) * mm});
            skLineSegment(sketch, "E376", {"start": v(13.38, -7.38) * mm, "end": v(13.38, -7.14) * mm});
            skLineSegment(sketch, "E377", {"start": v(13.38, -7.14) * mm, "end": v(13.5, -7.14) * mm});
            skLineSegment(sketch, "E378", {"start": v(13.5, -7.14) * mm, "end": v(13.5, -6.89) * mm});
            skLineSegment(sketch, "E379", {"start": v(13.5, -6.89) * mm, "end": v(13.63, -6.89) * mm});
            skLineSegment(sketch, "E380", {"start": v(13.63, -6.89) * mm, "end": v(13.63, -6.64) * mm});
            skLineSegment(sketch, "E381", {"start": v(13.63, -6.64) * mm, "end": v(13.76, -6.64) * mm});
            skLineSegment(sketch, "E382", {"start": v(13.76, -6.64) * mm, "end": v(13.88, -6.39) * mm});
            skLineSegment(sketch, "E383", {"start": v(13.88, -6.39) * mm, "end": v(14, -5.64) * mm});
            skLineSegment(sketch, "E384", {"start": v(14, -5.64) * mm, "end": v(14.25, -5.4) * mm});
            skLineSegment(sketch, "E385", {"start": v(14.25, -5.4) * mm, "end": v(14.25, -4.9) * mm});
            skLineSegment(sketch, "E386", {"start": v(14.25, -4.9) * mm, "end": v(14.5, -4.52) * mm});
            skLineSegment(sketch, "E387", {"start": v(14.5, -4.52) * mm, "end": v(14.5, -4.02) * mm});
            skLineSegment(sketch, "E388", {"start": v(14.5, -4.02) * mm, "end": v(14.63, -4.02) * mm});
            skLineSegment(sketch, "E389", {"start": v(14.63, -4.02) * mm, "end": v(14.63, -3.4) * mm});
            skLineSegment(sketch, "E390", {"start": v(14.63, -3.4) * mm, "end": v(14.75, -3.4) * mm});
            skLineSegment(sketch, "E391", {"start": v(14.75, -3.4) * mm, "end": v(14.75, -2.65) * mm});
            skLineSegment(sketch, "E392", {"start": v(14.75, -2.65) * mm, "end": v(14.88, -2.65) * mm});
            skLineSegment(sketch, "E393", {"start": v(14.88, -2.65) * mm, "end": v(14.88, -2.28) * mm});
            skLineSegment(sketch, "E394", {"start": v(14.88, -2.28) * mm, "end": v(14.88, -1.9) * mm});
            skLineSegment(sketch, "E395", {"start": v(14.88, -1.9) * mm, "end": v(14.88, -1.53) * mm});
            skLineSegment(sketch, "E396", {"start": v(14.88, -1.53) * mm, "end": v(15, -1.53) * mm});
            skLineSegment(sketch, "E397", {"start": v(15, -1.53) * mm, "end": v(15, -1.16) * mm});
            skLineSegment(sketch, "E398", {"start": v(15, -1.16) * mm, "end": v(15, -0.66) * mm});
            skLineSegment(sketch, "E399", {"start": v(15, -0.66) * mm, "end": v(15, -0.54) * mm});
            skLineSegment(sketch, "E400", {"start": v(15, -0.54) * mm, "end": v(15, -0.41) * mm});
            skLineSegment(sketch, "E401", {"start": v(15, -0.41) * mm, "end": v(15, -0.29) * mm});
            skLineSegment(sketch, "E402", {"start": v(15, -0.29) * mm, "end": v(15, 0.46) * mm});
            skLineSegment(sketch, "E403", {"start": v(15, 0.46) * mm, "end": v(14.88, 0.46) * mm});
            skLineSegment(sketch, "E404", {"start": v(14.88, 0.46) * mm, "end": v(14.88, 1.45) * mm});
            skLineSegment(sketch, "E405", {"start": v(14.88, 1.45) * mm, "end": v(14.75, 1.45) * mm});
            skLineSegment(sketch, "E406", {"start": v(14.75, 1.45) * mm, "end": v(14.75, 2.33) * mm});
            skLineSegment(sketch, "E407", {"start": v(14.75, 2.33) * mm, "end": v(14.63, 2.33) * mm});
            skLineSegment(sketch, "E408", {"start": v(14.63, 2.33) * mm, "end": v(14.63, 2.95) * mm});
            skLineSegment(sketch, "E409", {"start": v(14.63, 2.95) * mm, "end": v(14.5, 2.95) * mm});
            skLineSegment(sketch, "E410", {"start": v(14.5, 2.95) * mm, "end": v(14.5, 3.45) * mm});
            skLineSegment(sketch, "E411", {"start": v(14.5, 3.45) * mm, "end": v(14.38, 3.82) * mm});
            skLineSegment(sketch, "E412", {"start": v(14.38, 3.82) * mm, "end": v(14.25, 3.82) * mm});
            skLineSegment(sketch, "E413", {"start": v(14.25, 3.82) * mm, "end": v(14.25, 4.2) * mm});
            skLineSegment(sketch, "E414", {"start": v(14.25, 4.2) * mm, "end": v(14.13, 4.2) * mm});
            skLineSegment(sketch, "E415", {"start": v(14.13, 4.2) * mm, "end": v(14.13, 4.57) * mm});
            skLineSegment(sketch, "E416", {"start": v(14.13, 4.57) * mm, "end": v(14, 4.57) * mm});
            skLineSegment(sketch, "E417", {"start": v(14, 4.57) * mm, "end": v(14, 4.94) * mm});
            skLineSegment(sketch, "E418", {"start": v(14, 4.94) * mm, "end": v(13.63, 5.44) * mm});
            skLineSegment(sketch, "E419", {"start": v(13.63, 5.44) * mm, "end": v(13.63, 5.81) * mm});
            skLineSegment(sketch, "E420", {"start": v(13.63, 5.81) * mm, "end": v(13.5, 6.06) * mm});
            skLineSegment(sketch, "E421", {"start": v(13.5, 6.06) * mm, "end": v(13.26, 6.18) * mm});
            skLineSegment(sketch, "E422", {"start": v(13.26, 6.18) * mm, "end": v(13.26, 6.43) * mm});
            skLineSegment(sketch, "E423", {"start": v(13.26, 6.43) * mm, "end": v(13.13, 6.43) * mm});
            skLineSegment(sketch, "E424", {"start": v(13.13, 6.43) * mm, "end": v(13.13, 6.68) * mm});
            skLineSegment(sketch, "E425", {"start": v(13.13, 6.68) * mm, "end": v(13, 6.68) * mm});
            skLineSegment(sketch, "E426", {"start": v(13, 6.68) * mm, "end": v(13, 6.93) * mm});
            skLineSegment(sketch, "E427", {"start": v(13, 6.93) * mm, "end": v(12.88, 6.93) * mm});
            skLineSegment(sketch, "E428", {"start": v(12.88, 6.93) * mm, "end": v(12.88, 7.18) * mm});
            skLineSegment(sketch, "E429", {"start": v(12.88, 7.18) * mm, "end": v(12.63, 7.3) * mm});
            skLineSegment(sketch, "E430", {"start": v(12.63, 7.3) * mm, "end": v(12.51, 7.8) * mm});
            skLineSegment(sketch, "E431", {"start": v(12.51, 7.8) * mm, "end": v(12.14, 8.05) * mm});
            skLineSegment(sketch, "E432", {"start": v(12.14, 8.05) * mm, "end": v(12.14, 8.3) * mm});
            skLineSegment(sketch, "E433", {"start": v(12.14, 8.3) * mm, "end": v(11.76, 8.55) * mm});
            skLineSegment(sketch, "E434", {"start": v(11.76, 8.55) * mm, "end": v(11.76, 8.8) * mm});
            skLineSegment(sketch, "E435", {"start": v(11.76, 8.8) * mm, "end": v(11.64, 8.92) * mm});
            skLineSegment(sketch, "E436", {"start": v(11.64, 8.92) * mm, "end": v(11.14, 9.3) * mm});
            skLineSegment(sketch, "E437", {"start": v(11.14, 9.3) * mm, "end": v(11.14, 9.55) * mm});
            skLineSegment(sketch, "E438", {"start": v(11.14, 9.55) * mm, "end": v(11.02, 9.67) * mm});
            skLineSegment(sketch, "E439", {"start": v(11.02, 9.67) * mm, "end": v(10.77, 9.92) * mm});
            skLineSegment(sketch, "E440", {"start": v(10.77, 9.92) * mm, "end": v(10.64, 9.92) * mm});
            skLineSegment(sketch, "E441", {"start": v(10.64, 9.92) * mm, "end": v(10.64, 10.04) * mm});
            skLineSegment(sketch, "E442", {"start": v(10.64, 10.04) * mm, "end": v(10.52, 10.04) * mm});
            skLineSegment(sketch, "E443", {"start": v(10.52, 10.04) * mm, "end": v(10.02, 10.42) * mm});
            skLineSegment(sketch, "E444", {"start": v(10.02, 10.42) * mm, "end": v(9.9, 10.04) * mm});
            skLineSegment(sketch, "E445", {"start": v(9.9, 10.04) * mm, "end": v(9.65, 9.8) * mm});
            skLineSegment(sketch, "E446", {"start": v(9.65, 9.8) * mm, "end": v(9.52, 9.8) * mm});
            skLineSegment(sketch, "E447", {"start": v(9.52, 9.8) * mm, "end": v(9.52, 9.67) * mm});
            skLineSegment(sketch, "E448", {"start": v(9.52, 9.67) * mm, "end": v(9.4, 9.67) * mm});
            skLineSegment(sketch, "E449", {"start": v(9.4, 9.67) * mm, "end": v(9.02, 9.3) * mm});
            skLineSegment(sketch, "E450", {"start": v(9.02, 9.3) * mm, "end": v(9.02, 9.05) * mm});
            skLineSegment(sketch, "E451", {"start": v(9.02, 9.05) * mm, "end": v(8.9, 8.92) * mm});
            skLineSegment(sketch, "E452", {"start": v(8.9, 8.92) * mm, "end": v(8.28, 8.42) * mm});
            skLineSegment(sketch, "E453", {"start": v(8.28, 8.42) * mm, "end": v(8.28, 8.18) * mm});
            skLineSegment(sketch, "E454", {"start": v(8.28, 8.18) * mm, "end": v(8.15, 8.05) * mm});
            skLineSegment(sketch, "E455", {"start": v(8.15, 8.05) * mm, "end": v(7.53, 7.55) * mm});
            skLineSegment(sketch, "E456", {"start": v(7.53, 7.55) * mm, "end": v(7.53, 7.3) * mm});
            skLineSegment(sketch, "E457", {"start": v(7.53, 7.3) * mm, "end": v(7.28, 7.18) * mm});
            skLineSegment(sketch, "E458", {"start": v(7.28, 7.18) * mm, "end": v(7.28, 7.06) * mm});
            skLineSegment(sketch, "E459", {"start": v(7.28, 7.06) * mm, "end": v(7.53, 6.93) * mm});
            skLineSegment(sketch, "E460", {"start": v(7.53, 6.93) * mm, "end": v(7.53, 6.8) * mm});
            skLineSegment(sketch, "E461", {"start": v(7.53, 6.8) * mm, "end": v(7.66, 6.8) * mm});
            skLineSegment(sketch, "E462", {"start": v(7.66, 6.8) * mm, "end": v(7.66, 6.68) * mm});
            skLineSegment(sketch, "E463", {"start": v(7.66, 6.68) * mm, "end": v(7.78, 6.68) * mm});
            skLineSegment(sketch, "E464", {"start": v(7.78, 6.68) * mm, "end": v(7.78, 6.56) * mm});
            skLineSegment(sketch, "E465", {"start": v(7.78, 6.56) * mm, "end": v(7.9, 6.56) * mm});
            skLineSegment(sketch, "E466", {"start": v(7.9, 6.56) * mm, "end": v(7.9, 6.43) * mm});
            skLineSegment(sketch, "E467", {"start": v(7.9, 6.43) * mm, "end": v(8.15, 6.3) * mm});
            skLineSegment(sketch, "E468", {"start": v(8.15, 6.3) * mm, "end": v(8.15, 6.06) * mm});
            skLineSegment(sketch, "E469", {"start": v(8.15, 6.06) * mm, "end": v(8.53, 5.81) * mm});
            skLineSegment(sketch, "E470", {"start": v(8.53, 5.81) * mm, "end": v(8.53, 5.56) * mm});
            skLineSegment(sketch, "E471", {"start": v(8.53, 5.56) * mm, "end": v(8.78, 5.44) * mm});
            skLineSegment(sketch, "E472", {"start": v(8.78, 5.44) * mm, "end": v(8.78, 5.19) * mm});
            skLineSegment(sketch, "E473", {"start": v(8.78, 5.19) * mm, "end": v(9.02, 5.06) * mm});
            skLineSegment(sketch, "E474", {"start": v(9.02, 5.06) * mm, "end": v(9.15, 4.57) * mm});
            skLineSegment(sketch, "E475", {"start": v(9.15, 4.57) * mm, "end": v(9.4, 4.44) * mm});
            skLineSegment(sketch, "E476", {"start": v(9.4, 4.44) * mm, "end": v(9.52, 4.2) * mm});
            skLineSegment(sketch, "E477", {"start": v(9.52, 4.2) * mm, "end": v(9.52, 3.82) * mm});
            skLineSegment(sketch, "E478", {"start": v(9.52, 3.82) * mm, "end": v(9.65, 3.57) * mm});
            skLineSegment(sketch, "E479", {"start": v(9.65, 3.57) * mm, "end": v(9.77, 3.57) * mm});
            skLineSegment(sketch, "E480", {"start": v(9.77, 3.57) * mm, "end": v(9.9, 3.32) * mm});
            skLineSegment(sketch, "E481", {"start": v(9.9, 3.32) * mm, "end": v(10.02, 2.95) * mm});
            skLineSegment(sketch, "E482", {"start": v(10.02, 2.95) * mm, "end": v(10.02, 2.57) * mm});
            skLineSegment(sketch, "E483", {"start": v(10.02, 2.57) * mm, "end": v(10.15, 2.57) * mm});
            skLineSegment(sketch, "E484", {"start": v(10.15, 2.57) * mm, "end": v(10.15, 2.2) * mm});
            skLineSegment(sketch, "E485", {"start": v(10.15, 2.2) * mm, "end": v(10.27, 2.2) * mm});
            skLineSegment(sketch, "E486", {"start": v(10.27, 2.2) * mm, "end": v(10.27, 1.7) * mm});
            skLineSegment(sketch, "E487", {"start": v(10.27, 1.7) * mm, "end": v(10.4, 1.7) * mm});
            skLineSegment(sketch, "E488", {"start": v(10.4, 1.7) * mm, "end": v(10.4, 1.08) * mm});
            skLineSegment(sketch, "E489", {"start": v(10.4, 1.08) * mm, "end": v(10.52, 1.08) * mm});
            skLineSegment(sketch, "E490", {"start": v(10.52, 1.08) * mm, "end": v(10.52, 0.7) * mm});
            skLineSegment(sketch, "E491", {"start": v(10.52, 0.7) * mm, "end": v(10.52, 0.2) * mm});
            skLineSegment(sketch, "E492", {"start": v(10.52, 0.2) * mm, "end": v(10.52, 0.08) * mm});
            skLineSegment(sketch, "E493", {"start": v(10.52, 0.08) * mm, "end": v(10.52, -0.04) * mm});
            skLineSegment(sketch, "E494", {"start": v(10.52, -0.04) * mm, "end": v(10.52, -0.16) * mm});
            skLineSegment(sketch, "E495", {"start": v(10.52, -0.16) * mm, "end": v(10.52, -0.29) * mm});
            skLineSegment(sketch, "E496", {"start": v(10.52, -0.29) * mm, "end": v(10.52, -0.41) * mm});
            skLineSegment(sketch, "E497", {"start": v(10.52, -0.41) * mm, "end": v(10.52, -0.54) * mm});
            skLineSegment(sketch, "E498", {"start": v(10.52, -0.54) * mm, "end": v(10.52, -0.66) * mm});
            skLineSegment(sketch, "E499", {"start": v(10.52, -0.66) * mm, "end": v(10.52, -0.79) * mm});
            skLineSegment(sketch, "E500", {"start": v(10.52, -0.79) * mm, "end": v(10.52, -0.91) * mm});
            skLineSegment(sketch, "E501", {"start": v(10.52, -0.91) * mm, "end": v(10.52, -1.04) * mm});
            skLineSegment(sketch, "E502", {"start": v(10.52, -1.04) * mm, "end": v(10.52, -1.16) * mm});
            skLineSegment(sketch, "E503", {"start": v(10.52, -1.16) * mm, "end": v(10.52, -1.28) * mm});
            skLineSegment(sketch, "E504", {"start": v(10.52, -1.28) * mm, "end": v(10.52, -1.4) * mm});
            skLineSegment(sketch, "E505", {"start": v(10.52, -1.4) * mm, "end": v(10.52, -1.53) * mm});
            skLineSegment(sketch, "E506", {"start": v(10.52, -1.53) * mm, "end": v(10.52, -1.66) * mm});
            skLineSegment(sketch, "E507", {"start": v(10.52, -1.66) * mm, "end": v(10.52, -2.16) * mm});
            skLineSegment(sketch, "E508", {"start": v(10.52, -2.16) * mm, "end": v(10.4, -2.16) * mm});
            skLineSegment(sketch, "E509", {"start": v(10.4, -2.16) * mm, "end": v(10.4, -2.9) * mm});
            skLineSegment(sketch, "E510", {"start": v(10.4, -2.9) * mm, "end": v(10.27, -2.9) * mm});
            skLineSegment(sketch, "E511", {"start": v(10.27, -2.9) * mm, "end": v(10.27, -3.4) * mm});
            skLineSegment(sketch, "E512", {"start": v(10.27, -3.4) * mm, "end": v(10.15, -3.77) * mm});
            skLineSegment(sketch, "E513", {"start": v(10.15, -3.77) * mm, "end": v(10.02, -3.77) * mm});
            skLineSegment(sketch, "E514", {"start": v(10.02, -3.77) * mm, "end": v(10.02, -4.15) * mm});
            skLineSegment(sketch, "E515", {"start": v(10.02, -4.15) * mm, "end": v(9.9, -4.15) * mm});
            skLineSegment(sketch, "E516", {"start": v(9.9, -4.15) * mm, "end": v(9.9, -4.52) * mm});
            skLineSegment(sketch, "E517", {"start": v(9.9, -4.52) * mm, "end": v(9.65, -4.77) * mm});
            skLineSegment(sketch, "E518", {"start": v(9.65, -4.77) * mm, "end": v(9.65, -5.02) * mm});
            skLineSegment(sketch, "E519", {"start": v(9.65, -5.02) * mm, "end": v(9.52, -5.02) * mm});
            skLineSegment(sketch, "E520", {"start": v(9.52, -5.02) * mm, "end": v(9.27, -5.64) * mm});
            skLineSegment(sketch, "E521", {"start": v(9.27, -5.64) * mm, "end": v(9.02, -5.4) * mm});
            skLineSegment(sketch, "E522", {"start": v(9.02, -5.4) * mm, "end": v(8.9, -5.4) * mm});
            skLineSegment(sketch, "E523", {"start": v(8.9, -5.4) * mm, "end": v(8.9, -5.27) * mm});
            skLineSegment(sketch, "E524", {"start": v(8.9, -5.27) * mm, "end": v(8.78, -5.27) * mm});
            skLineSegment(sketch, "E525", {"start": v(8.78, -5.27) * mm, "end": v(8.78, -5.14) * mm});
            skLineSegment(sketch, "E526", {"start": v(8.78, -5.14) * mm, "end": v(8.65, -5.14) * mm});
            skLineSegment(sketch, "E527", {"start": v(8.65, -5.14) * mm, "end": v(8.65, -5.02) * mm});
            skLineSegment(sketch, "E528", {"start": v(8.65, -5.02) * mm, "end": v(8.53, -5.02) * mm});
            skLineSegment(sketch, "E529", {"start": v(8.53, -5.02) * mm, "end": v(8.53, -4.9) * mm});
            skLineSegment(sketch, "E530", {"start": v(8.53, -4.9) * mm, "end": v(8.4, -4.9) * mm});
            skLineSegment(sketch, "E531", {"start": v(8.4, -4.9) * mm, "end": v(8.4, -4.77) * mm});
            skLineSegment(sketch, "E532", {"start": v(8.4, -4.77) * mm, "end": v(8.28, -4.77) * mm});
            skLineSegment(sketch, "E533", {"start": v(8.28, -4.77) * mm, "end": v(8.28, -4.65) * mm});
            skLineSegment(sketch, "E534", {"start": v(8.28, -4.65) * mm, "end": v(8.15, -4.65) * mm});
            skLineSegment(sketch, "E535", {"start": v(8.15, -4.65) * mm, "end": v(8.15, -4.52) * mm});
            skLineSegment(sketch, "E536", {"start": v(8.15, -4.52) * mm, "end": v(8.03, -4.52) * mm});
            skLineSegment(sketch, "E537", {"start": v(8.03, -4.52) * mm, "end": v(8.03, -4.4) * mm});
            skLineSegment(sketch, "E538", {"start": v(8.03, -4.4) * mm, "end": v(7.9, -4.4) * mm});
            skLineSegment(sketch, "E539", {"start": v(7.9, -4.4) * mm, "end": v(7.9, -4.27) * mm});
            skLineSegment(sketch, "E540", {"start": v(7.9, -4.27) * mm, "end": v(7.78, -4.27) * mm});
            skLineSegment(sketch, "E541", {"start": v(7.78, -4.27) * mm, "end": v(7.53, -3.9) * mm});
            skLineSegment(sketch, "E542", {"start": v(7.53, -3.9) * mm, "end": v(7.28, -3.9) * mm});
            skLineSegment(sketch, "E543", {"start": v(7.28, -3.9) * mm, "end": v(7.16, -3.77) * mm});
            skLineSegment(sketch, "E544", {"start": v(7.16, -3.77) * mm, "end": v(6.9, -3.53) * mm});
            skLineSegment(sketch, "E545", {"start": v(6.9, -3.53) * mm, "end": v(6.9, -3.4) * mm});
            skLineSegment(sketch, "E546", {"start": v(6.9, -3.4) * mm, "end": v(6.78, -3.4) * mm});
            skLineSegment(sketch, "E547", {"start": v(6.78, -3.4) * mm, "end": v(6.78, -3.28) * mm});
            skLineSegment(sketch, "E548", {"start": v(6.78, -3.28) * mm, "end": v(6.66, -3.28) * mm});
            skLineSegment(sketch, "E549", {"start": v(6.66, -3.28) * mm, "end": v(6.66, -3.15) * mm});
            skLineSegment(sketch, "E550", {"start": v(6.66, -3.15) * mm, "end": v(6.54, -3.15) * mm});
            skLineSegment(sketch, "E551", {"start": v(6.54, -3.15) * mm, "end": v(6.54, -3.03) * mm});
            skLineSegment(sketch, "E552", {"start": v(6.54, -3.03) * mm, "end": v(6.41, -3.03) * mm});
            skLineSegment(sketch, "E553", {"start": v(6.41, -3.03) * mm, "end": v(6.41, -2.9) * mm});
            skLineSegment(sketch, "E554", {"start": v(6.41, -2.9) * mm, "end": v(6.29, -2.9) * mm});
            skLineSegment(sketch, "E555", {"start": v(6.29, -2.9) * mm, "end": v(6.29, -2.78) * mm});
            skLineSegment(sketch, "E556", {"start": v(6.29, -2.78) * mm, "end": v(6.16, -2.78) * mm});
            skLineSegment(sketch, "E557", {"start": v(6.16, -2.78) * mm, "end": v(6.16, -2.65) * mm});
            skLineSegment(sketch, "E558", {"start": v(6.16, -2.65) * mm, "end": v(6.04, -2.65) * mm});
            skLineSegment(sketch, "E559", {"start": v(6.04, -2.65) * mm, "end": v(6.04, -2.53) * mm});
            skLineSegment(sketch, "E560", {"start": v(6.04, -2.53) * mm, "end": v(5.91, -2.53) * mm});
            skLineSegment(sketch, "E561", {"start": v(5.91, -2.53) * mm, "end": v(5.91, -2.4) * mm});
            skLineSegment(sketch, "E562", {"start": v(5.91, -2.4) * mm, "end": v(5.79, -2.4) * mm});
            skLineSegment(sketch, "E563", {"start": v(5.79, -2.4) * mm, "end": v(5.79, -2.28) * mm});
            skLineSegment(sketch, "E564", {"start": v(5.79, -2.28) * mm, "end": v(5.66, -2.28) * mm});
            skLineSegment(sketch, "E565", {"start": v(5.66, -2.28) * mm, "end": v(5.66, -2.16) * mm});
            skLineSegment(sketch, "E566", {"start": v(5.66, -2.16) * mm, "end": v(5.54, -2.16) * mm});
            skLineSegment(sketch, "E567", {"start": v(5.54, -2.16) * mm, "end": v(5.54, -2.03) * mm});
            skLineSegment(sketch, "E568", {"start": v(5.54, -2.03) * mm, "end": v(5.41, -2.03) * mm});
            skLineSegment(sketch, "E569", {"start": v(5.41, -2.03) * mm, "end": v(5.41, -1.9) * mm});
            skLineSegment(sketch, "E570", {"start": v(5.41, -1.9) * mm, "end": v(5.3, -1.9) * mm});
            skLineSegment(sketch, "E571", {"start": v(5.3, -1.9) * mm, "end": v(5.3, -1.78) * mm});
            skLineSegment(sketch, "E572", {"start": v(5.3, -1.78) * mm, "end": v(5.17, -1.78) * mm});
            skLineSegment(sketch, "E573", {"start": v(5.17, -1.78) * mm, "end": v(5.17, -1.66) * mm});
            skLineSegment(sketch, "E574", {"start": v(5.17, -1.66) * mm, "end": v(5.04, -1.66) * mm});
            skLineSegment(sketch, "E575", {"start": v(5.04, -1.66) * mm, "end": v(5.04, -1.53) * mm});
            skLineSegment(sketch, "E576", {"start": v(5.04, -1.53) * mm, "end": v(4.92, -1.53) * mm});
            skLineSegment(sketch, "E577", {"start": v(4.92, -1.53) * mm, "end": v(4.92, -1.4) * mm});
            skLineSegment(sketch, "E578", {"start": v(4.92, -1.4) * mm, "end": v(4.8, -1.4) * mm});
            skLineSegment(sketch, "E579", {"start": v(4.8, -1.4) * mm, "end": v(4.8, -1.28) * mm});
            skLineSegment(sketch, "E580", {"start": v(4.8, -1.28) * mm, "end": v(4.67, -1.28) * mm});
            skLineSegment(sketch, "E581", {"start": v(4.67, -1.28) * mm, "end": v(4.67, -1.16) * mm});
            skLineSegment(sketch, "E582", {"start": v(4.67, -1.16) * mm, "end": v(4.54, -1.16) * mm});
            skLineSegment(sketch, "E583", {"start": v(4.54, -1.16) * mm, "end": v(4.54, -1.04) * mm});
            skLineSegment(sketch, "E584", {"start": v(4.54, -1.04) * mm, "end": v(4.42, -1.04) * mm});
            skLineSegment(sketch, "E585", {"start": v(4.42, -1.04) * mm, "end": v(4.42, -0.91) * mm});
            skLineSegment(sketch, "E586", {"start": v(4.42, -0.91) * mm, "end": v(4.3, -0.91) * mm});
            skLineSegment(sketch, "E587", {"start": v(4.3, -0.91) * mm, "end": v(4.3, -0.79) * mm});
            skLineSegment(sketch, "E588", {"start": v(4.3, -0.79) * mm, "end": v(4.17, -0.79) * mm});
            skLineSegment(sketch, "E589", {"start": v(4.17, -0.79) * mm, "end": v(4.17, -0.66) * mm});
            skLineSegment(sketch, "E590", {"start": v(4.17, -0.66) * mm, "end": v(4.05, -0.66) * mm});
            skLineSegment(sketch, "E591", {"start": v(4.05, -0.66) * mm, "end": v(4.05, -0.54) * mm});
            skLineSegment(sketch, "E592", {"start": v(4.05, -0.54) * mm, "end": v(3.92, -0.41) * mm});
            skLineSegment(sketch, "E593", {"start": v(3.92, -0.41) * mm, "end": v(3.8, -0.29) * mm});
            skLineSegment(sketch, "E594", {"start": v(3.8, -0.29) * mm, "end": v(3.55, -0.29) * mm});
            skLineSegment(sketch, "E595", {"start": v(3.55, -0.29) * mm, "end": v(3.42, 0.2) * mm});
            skLineSegment(sketch, "E596", {"start": v(3.42, 0.2) * mm, "end": v(3.3, 0.2) * mm});
            skLineSegment(sketch, "E597", {"start": v(3.3, 0.2) * mm, "end": v(3.3, 0.46) * mm});
            skLineSegment(sketch, "E598", {"start": v(3.3, 0.46) * mm, "end": v(3.05, 0.7) * mm});
            skLineSegment(sketch, "E599", {"start": v(3.05, 0.7) * mm, "end": v(3.05, 1.08) * mm});
            skLineSegment(sketch, "E600", {"start": v(3.05, 1.08) * mm, "end": v(2.93, 1.33) * mm});
            skLineSegment(sketch, "E601", {"start": v(2.93, 1.33) * mm, "end": v(2.8, 1.33) * mm});
            skLineSegment(sketch, "E602", {"start": v(2.8, 1.33) * mm, "end": v(2.8, 1.58) * mm});
            skLineSegment(sketch, "E603", {"start": v(2.8, 1.58) * mm, "end": v(2.68, 1.58) * mm});
            skLineSegment(sketch, "E604", {"start": v(2.68, 1.58) * mm, "end": v(2.68, 1.83) * mm});
            skLineSegment(sketch, "E605", {"start": v(2.68, 1.83) * mm, "end": v(2.55, 1.83) * mm});
            skLineSegment(sketch, "E606", {"start": v(2.55, 1.83) * mm, "end": v(2.43, 2.08) * mm});
            skLineSegment(sketch, "E607", {"start": v(2.43, 2.08) * mm, "end": v(2.43, 2.45) * mm});
            skLineSegment(sketch, "E608", {"start": v(2.43, 2.45) * mm, "end": v(2.3, 2.7) * mm});
            skLineSegment(sketch, "E609", {"start": v(2.3, 2.7) * mm, "end": v(2.18, 2.7) * mm});
            skLineSegment(sketch, "E610", {"start": v(2.18, 2.7) * mm, "end": v(2.18, 2.95) * mm});
            skLineSegment(sketch, "E611", {"start": v(2.18, 2.95) * mm, "end": v(2.05, 2.95) * mm});
            skLineSegment(sketch, "E612", {"start": v(2.05, 2.95) * mm, "end": v(2.05, 3.2) * mm});
            skLineSegment(sketch, "E613", {"start": v(2.05, 3.2) * mm, "end": v(1.93, 3.2) * mm});
            skLineSegment(sketch, "E614", {"start": v(1.93, 3.2) * mm, "end": v(1.93, 3.45) * mm});
            skLineSegment(sketch, "E615", {"start": v(1.93, 3.45) * mm, "end": v(1.8, 3.45) * mm});
            skLineSegment(sketch, "E616", {"start": v(1.8, 3.45) * mm, "end": v(1.8, 3.7) * mm});
            skLineSegment(sketch, "E617", {"start": v(1.8, 3.7) * mm, "end": v(1.56, 3.94) * mm});
            skLineSegment(sketch, "E618", {"start": v(1.56, 3.94) * mm, "end": v(1.56, 4.32) * mm});
            skLineSegment(sketch, "E619", {"start": v(1.56, 4.32) * mm, "end": v(1.43, 4.57) * mm});
            skLineSegment(sketch, "E620", {"start": v(1.43, 4.57) * mm, "end": v(1.3, 4.57) * mm});
            skLineSegment(sketch, "E621", {"start": v(1.3, 4.57) * mm, "end": v(1.3, 4.81) * mm});
            skLineSegment(sketch, "E622", {"start": v(1.3, 4.81) * mm, "end": v(1.18, 4.81) * mm});
            skLineSegment(sketch, "E623", {"start": v(1.18, 4.81) * mm, "end": v(1.18, 5.06) * mm});
            skLineSegment(sketch, "E624", {"start": v(1.18, 5.06) * mm, "end": v(1.06, 5.06) * mm});
            skLineSegment(sketch, "E625", {"start": v(1.06, 5.06) * mm, "end": v(1.06, 5.31) * mm});
            skLineSegment(sketch, "E626", {"start": v(1.06, 5.31) * mm, "end": v(0.93, 5.31) * mm});
            skLineSegment(sketch, "E627", {"start": v(0.93, 5.31) * mm, "end": v(0.68, 6.06) * mm});
            skLineSegment(sketch, "E628", {"start": v(0.68, 6.06) * mm, "end": v(0.56, 6.06) * mm});
            skLineSegment(sketch, "E629", {"start": v(0.56, 6.06) * mm, "end": v(0.56, 5.56) * mm});
            skLineSegment(sketch, "E630", {"start": v(0.56, 5.56) * mm, "end": v(0.56, 5.44) * mm});
            skLineSegment(sketch, "E631", {"start": v(0.56, 5.44) * mm, "end": v(0.56, 5.31) * mm});
            skLineSegment(sketch, "E632", {"start": v(0.56, 5.31) * mm, "end": v(0.56, 5.19) * mm});
            skLineSegment(sketch, "E633", {"start": v(0.56, 5.19) * mm, "end": v(0.56, 5.06) * mm});
            skLineSegment(sketch, "E634", {"start": v(0.56, 5.06) * mm, "end": v(0.56, 4.94) * mm});
            skLineSegment(sketch, "E635", {"start": v(0.56, 4.94) * mm, "end": v(0.56, 4.81) * mm});
            skLineSegment(sketch, "E636", {"start": v(0.56, 4.81) * mm, "end": v(0.56, 4.7) * mm});
            skLineSegment(sketch, "E637", {"start": v(0.56, 4.7) * mm, "end": v(0.56, 4.57) * mm});
            skLineSegment(sketch, "E638", {"start": v(0.56, 4.57) * mm, "end": v(0.56, 4.44) * mm});
            skLineSegment(sketch, "E639", {"start": v(0.56, 4.44) * mm, "end": v(0.56, 4.32) * mm});
            skLineSegment(sketch, "E640", {"start": v(0.56, 4.32) * mm, "end": v(0.56, 4.2) * mm});
            skLineSegment(sketch, "E641", {"start": v(0.56, 4.2) * mm, "end": v(0.56, 4.07) * mm});
            skLineSegment(sketch, "E642", {"start": v(0.56, 4.07) * mm, "end": v(0.56, 3.94) * mm});
            skLineSegment(sketch, "E643", {"start": v(0.56, 3.94) * mm, "end": v(0.56, 3.82) * mm});
            skLineSegment(sketch, "E644", {"start": v(0.56, 3.82) * mm, "end": v(0.56, 3.7) * mm});
            skLineSegment(sketch, "E645", {"start": v(0.56, 3.7) * mm, "end": v(0.56, 3.57) * mm});
            skLineSegment(sketch, "E646", {"start": v(0.56, 3.57) * mm, "end": v(0.56, 3.45) * mm});
            skLineSegment(sketch, "E647", {"start": v(0.56, 3.45) * mm, "end": v(0.56, 3.32) * mm});
            skLineSegment(sketch, "E648", {"start": v(0.56, 3.32) * mm, "end": v(0.56, 3.2) * mm});
            skLineSegment(sketch, "E649", {"start": v(0.56, 3.2) * mm, "end": v(0.56, 3.07) * mm});
            skLineSegment(sketch, "E650", {"start": v(0.56, 3.07) * mm, "end": v(0.56, 2.95) * mm});
            skLineSegment(sketch, "E651", {"start": v(0.56, 2.95) * mm, "end": v(0.56, 2.82) * mm});
            skLineSegment(sketch, "E652", {"start": v(0.56, 2.82) * mm, "end": v(0.56, 2.7) * mm});
            skLineSegment(sketch, "E653", {"start": v(0.56, 2.7) * mm, "end": v(0.56, 2.57) * mm});
            skLineSegment(sketch, "E654", {"start": v(0.56, 2.57) * mm, "end": v(0.56, 2.45) * mm});
            skLineSegment(sketch, "E655", {"start": v(0.56, 2.45) * mm, "end": v(0.56, 2.33) * mm});
            skLineSegment(sketch, "E656", {"start": v(0.56, 2.33) * mm, "end": v(0.56, 2.2) * mm});
            skLineSegment(sketch, "E657", {"start": v(0.56, 2.2) * mm, "end": v(0.56, 2.08) * mm});
            skLineSegment(sketch, "E658", {"start": v(0.56, 2.08) * mm, "end": v(0.56, 1.95) * mm});
            skLineSegment(sketch, "E659", {"start": v(0.56, 1.95) * mm, "end": v(0.56, 1.83) * mm});
            skLineSegment(sketch, "E660", {"start": v(0.56, 1.83) * mm, "end": v(0.56, 1.7) * mm});
            skLineSegment(sketch, "E661", {"start": v(0.56, 1.7) * mm, "end": v(0.56, 1.58) * mm});
            skLineSegment(sketch, "E662", {"start": v(0.56, 1.58) * mm, "end": v(0.56, 1.45) * mm});
            skLineSegment(sketch, "E663", {"start": v(0.56, 1.45) * mm, "end": v(0.56, 1.33) * mm});
            skLineSegment(sketch, "E664", {"start": v(0.56, 1.33) * mm, "end": v(0.56, 1.2) * mm});
            skLineSegment(sketch, "E665", {"start": v(0.56, 1.2) * mm, "end": v(0.56, 1.08) * mm});
            skLineSegment(sketch, "E666", {"start": v(0.56, 1.08) * mm, "end": v(0.56, 0.96) * mm});
            skLineSegment(sketch, "E667", {"start": v(0.56, 0.96) * mm, "end": v(0.56, 0.83) * mm});
            skLineSegment(sketch, "E668", {"start": v(0.56, 0.83) * mm, "end": v(0.56, 0.7) * mm});
            skLineSegment(sketch, "E669", {"start": v(0.56, 0.7) * mm, "end": v(0.56, 0.58) * mm});
            skLineSegment(sketch, "E670", {"start": v(0.56, 0.58) * mm, "end": v(0.56, 0.46) * mm});
            skLineSegment(sketch, "E671", {"start": v(0.56, 0.46) * mm, "end": v(0.56, 0.33) * mm});
            skLineSegment(sketch, "E672", {"start": v(0.56, 0.33) * mm, "end": v(0.56, 0.2) * mm});
            skLineSegment(sketch, "E673", {"start": v(0.56, 0.2) * mm, "end": v(0.56, 0.08) * mm});
            skLineSegment(sketch, "E674", {"start": v(0.56, 0.08) * mm, "end": v(0.56, -0.04) * mm});
            skLineSegment(sketch, "E675", {"start": v(0.56, -0.04) * mm, "end": v(0.56, -0.16) * mm});
            skLineSegment(sketch, "E676", {"start": v(0.56, -0.16) * mm, "end": v(0.56, -0.29) * mm});
            skLineSegment(sketch, "E677", {"start": v(0.56, -0.29) * mm, "end": v(0.56, -0.41) * mm});
            skLineSegment(sketch, "E678", {"start": v(0.56, -0.41) * mm, "end": v(0.56, -0.54) * mm});
            skLineSegment(sketch, "E679", {"start": v(0.56, -0.54) * mm, "end": v(0.56, -0.66) * mm});
            skLineSegment(sketch, "E680", {"start": v(0.56, -0.66) * mm, "end": v(0.56, -0.79) * mm});
            skLineSegment(sketch, "E681", {"start": v(0.56, -0.79) * mm, "end": v(0.56, -0.91) * mm});
            skLineSegment(sketch, "E682", {"start": v(0.56, -0.91) * mm, "end": v(0.56, -1.04) * mm});
            skLineSegment(sketch, "E683", {"start": v(0.56, -1.04) * mm, "end": v(0.56, -1.16) * mm});
            skLineSegment(sketch, "E684", {"start": v(0.56, -1.16) * mm, "end": v(0.56, -1.28) * mm});
            skLineSegment(sketch, "E685", {"start": v(0.56, -1.28) * mm, "end": v(0.56, -1.4) * mm});
            skLineSegment(sketch, "E686", {"start": v(0.56, -1.4) * mm, "end": v(0.56, -1.53) * mm});
            skLineSegment(sketch, "E687", {"start": v(0.56, -1.53) * mm, "end": v(0.56, -1.66) * mm});
            skLineSegment(sketch, "E688", {"start": v(0.56, -1.66) * mm, "end": v(0.56, -1.78) * mm});
            skLineSegment(sketch, "E689", {"start": v(0.56, -1.78) * mm, "end": v(0.56, -1.9) * mm});
            skLineSegment(sketch, "E690", {"start": v(0.56, -1.9) * mm, "end": v(0.56, -2.03) * mm});
            skLineSegment(sketch, "E691", {"start": v(0.56, -2.03) * mm, "end": v(0.56, -2.16) * mm});
            skLineSegment(sketch, "E692", {"start": v(0.56, -2.16) * mm, "end": v(0.56, -2.28) * mm});
            skLineSegment(sketch, "E693", {"start": v(0.56, -2.28) * mm, "end": v(0.56, -2.4) * mm});
            skLineSegment(sketch, "E694", {"start": v(0.56, -2.4) * mm, "end": v(0.56, -2.53) * mm});
            skLineSegment(sketch, "E695", {"start": v(0.56, -2.53) * mm, "end": v(0.56, -2.65) * mm});
            skLineSegment(sketch, "E696", {"start": v(0.56, -2.65) * mm, "end": v(0.56, -2.78) * mm});
            skLineSegment(sketch, "E697", {"start": v(0.56, -2.78) * mm, "end": v(0.56, -3.4) * mm});
            skLineSegment(sketch, "E698", {"start": v(0.56, -3.4) * mm, "end": v(0.8, -3.65) * mm});
            skLineSegment(sketch, "E699", {"start": v(0.8, -3.65) * mm, "end": v(0.93, -3.65) * mm});
            skLineSegment(sketch, "E700", {"start": v(0.93, -3.65) * mm, "end": v(0.93, -3.77) * mm});
            skLineSegment(sketch, "E701", {"start": v(0.93, -3.77) * mm, "end": v(1.06, -3.77) * mm});
            skLineSegment(sketch, "E702", {"start": v(1.06, -3.77) * mm, "end": v(1.06, -3.9) * mm});
            skLineSegment(sketch, "E703", {"start": v(1.06, -3.9) * mm, "end": v(1.18, -3.9) * mm});
            skLineSegment(sketch, "E704", {"start": v(1.18, -3.9) * mm, "end": v(1.18, -4.02) * mm});
            skLineSegment(sketch, "E705", {"start": v(1.18, -4.02) * mm, "end": v(1.3, -4.02) * mm});
            skLineSegment(sketch, "E706", {"start": v(1.3, -4.02) * mm, "end": v(1.3, -4.15) * mm});
            skLineSegment(sketch, "E707", {"start": v(1.3, -4.15) * mm, "end": v(1.43, -4.15) * mm});
            skLineSegment(sketch, "E708", {"start": v(1.43, -4.15) * mm, "end": v(1.43, -4.27) * mm});
            skLineSegment(sketch, "E709", {"start": v(1.43, -4.27) * mm, "end": v(1.56, -4.27) * mm});
            skLineSegment(sketch, "E710", {"start": v(1.56, -4.27) * mm, "end": v(1.56, -4.4) * mm});
            skLineSegment(sketch, "E711", {"start": v(1.56, -4.4) * mm, "end": v(1.68, -4.4) * mm});
            skLineSegment(sketch, "E712", {"start": v(1.68, -4.4) * mm, "end": v(1.68, -4.52) * mm});
            skLineSegment(sketch, "E713", {"start": v(1.68, -4.52) * mm, "end": v(1.8, -4.52) * mm});
            skLineSegment(sketch, "E714", {"start": v(1.8, -4.52) * mm, "end": v(1.8, -4.65) * mm});
            skLineSegment(sketch, "E715", {"start": v(1.8, -4.65) * mm, "end": v(1.93, -4.65) * mm});
            skLineSegment(sketch, "E716", {"start": v(1.93, -4.65) * mm, "end": v(1.93, -4.77) * mm});
            skLineSegment(sketch, "E717", {"start": v(1.93, -4.77) * mm, "end": v(2.05, -4.77) * mm});
            skLineSegment(sketch, "E718", {"start": v(2.05, -4.77) * mm, "end": v(2.05, -4.9) * mm});
            skLineSegment(sketch, "E719", {"start": v(2.05, -4.9) * mm, "end": v(2.18, -4.9) * mm});
            skLineSegment(sketch, "E720", {"start": v(2.18, -4.9) * mm, "end": v(2.18, -5.02) * mm});
            skLineSegment(sketch, "E721", {"start": v(2.18, -5.02) * mm, "end": v(2.3, -5.02) * mm});
            skLineSegment(sketch, "E722", {"start": v(2.3, -5.02) * mm, "end": v(2.3, -5.14) * mm});
            skLineSegment(sketch, "E723", {"start": v(2.3, -5.14) * mm, "end": v(2.43, -5.14) * mm});
            skLineSegment(sketch, "E724", {"start": v(2.43, -5.14) * mm, "end": v(2.43, -5.27) * mm});
            skLineSegment(sketch, "E725", {"start": v(2.43, -5.27) * mm, "end": v(2.55, -5.27) * mm});
            skLineSegment(sketch, "E726", {"start": v(2.55, -5.27) * mm, "end": v(2.55, -5.4) * mm});
            skLineSegment(sketch, "E727", {"start": v(2.55, -5.4) * mm, "end": v(2.68, -5.4) * mm});
            skLineSegment(sketch, "E728", {"start": v(2.68, -5.4) * mm, "end": v(2.68, -5.52) * mm});
            skLineSegment(sketch, "E729", {"start": v(2.68, -5.52) * mm, "end": v(2.8, -5.52) * mm});
            skLineSegment(sketch, "E730", {"start": v(2.8, -5.52) * mm, "end": v(2.8, -5.64) * mm});
            skLineSegment(sketch, "E731", {"start": v(2.8, -5.64) * mm, "end": v(2.93, -5.64) * mm});
            skLineSegment(sketch, "E732", {"start": v(2.93, -5.64) * mm, "end": v(2.93, -5.77) * mm});
            skLineSegment(sketch, "E733", {"start": v(2.93, -5.77) * mm, "end": v(3.05, -5.77) * mm});
            skLineSegment(sketch, "E734", {"start": v(3.05, -5.77) * mm, "end": v(3.05, -5.9) * mm});
            skLineSegment(sketch, "E735", {"start": v(3.05, -5.9) * mm, "end": v(3.17, -5.9) * mm});
            skLineSegment(sketch, "E736", {"start": v(3.17, -5.9) * mm, "end": v(3.17, -6.01) * mm});
            skLineSegment(sketch, "E737", {"start": v(3.17, -6.01) * mm, "end": v(3.3, -6.01) * mm});
            skLineSegment(sketch, "E738", {"start": v(3.3, -6.01) * mm, "end": v(3.3, -6.14) * mm});
            skLineSegment(sketch, "E739", {"start": v(3.3, -6.14) * mm, "end": v(3.42, -6.14) * mm});
            skLineSegment(sketch, "E740", {"start": v(3.42, -6.14) * mm, "end": v(3.42, -6.26) * mm});
            skLineSegment(sketch, "E741", {"start": v(3.42, -6.26) * mm, "end": v(3.55, -6.26) * mm});
            skLineSegment(sketch, "E742", {"start": v(3.55, -6.26) * mm, "end": v(3.55, -6.39) * mm});
            skLineSegment(sketch, "E743", {"start": v(3.55, -6.39) * mm, "end": v(3.67, -6.39) * mm});
            skLineSegment(sketch, "E744", {"start": v(3.67, -6.39) * mm, "end": v(3.67, -6.51) * mm});
            skLineSegment(sketch, "E745", {"start": v(3.67, -6.51) * mm, "end": v(3.8, -6.51) * mm});
            skLineSegment(sketch, "E746", {"start": v(3.8, -6.51) * mm, "end": v(4.05, -6.89) * mm});
            skLineSegment(sketch, "E747", {"start": v(4.05, -6.89) * mm, "end": v(4.3, -6.89) * mm});
            skLineSegment(sketch, "E748", {"start": v(4.3, -6.89) * mm, "end": v(4.42, -7.01) * mm});
            skLineSegment(sketch, "E749", {"start": v(4.42, -7.01) * mm, "end": v(4.67, -7.26) * mm});
            skLineSegment(sketch, "E750", {"start": v(4.67, -7.26) * mm, "end": v(4.67, -7.38) * mm});
            skLineSegment(sketch, "E751", {"start": v(4.67, -7.38) * mm, "end": v(4.8, -7.38) * mm});
            skLineSegment(sketch, "E752", {"start": v(4.8, -7.38) * mm, "end": v(4.8, -7.5) * mm});
            skLineSegment(sketch, "E753", {"start": v(4.8, -7.5) * mm, "end": v(4.92, -7.5) * mm});
            skLineSegment(sketch, "E754", {"start": v(4.92, -7.5) * mm, "end": v(4.92, -7.63) * mm});
            skLineSegment(sketch, "E755", {"start": v(4.92, -7.63) * mm, "end": v(5.04, -7.63) * mm});
            skLineSegment(sketch, "E756", {"start": v(5.04, -7.63) * mm, "end": v(5.04, -7.76) * mm});
            skLineSegment(sketch, "E757", {"start": v(5.04, -7.76) * mm, "end": v(5.17, -7.76) * mm});
            skLineSegment(sketch, "E758", {"start": v(5.17, -7.76) * mm, "end": v(5.17, -7.88) * mm});
            skLineSegment(sketch, "E759", {"start": v(5.17, -7.88) * mm, "end": v(5.3, -7.88) * mm});
            skLineSegment(sketch, "E760", {"start": v(5.3, -7.88) * mm, "end": v(5.3, -8) * mm});
            skLineSegment(sketch, "E761", {"start": v(5.3, -8) * mm, "end": v(5.41, -8) * mm});
            skLineSegment(sketch, "E762", {"start": v(5.41, -8) * mm, "end": v(5.41, -8.13) * mm});
            skLineSegment(sketch, "E763", {"start": v(5.41, -8.13) * mm, "end": v(5.54, -8.13) * mm});
            skLineSegment(sketch, "E764", {"start": v(5.54, -8.13) * mm, "end": v(5.54, -8.26) * mm});
            skLineSegment(sketch, "E765", {"start": v(5.54, -8.26) * mm, "end": v(5.66, -8.26) * mm});
            skLineSegment(sketch, "E766", {"start": v(5.66, -8.26) * mm, "end": v(5.66, -8.38) * mm});
            skLineSegment(sketch, "E767", {"start": v(5.66, -8.38) * mm, "end": v(5.79, -8.38) * mm});
            skLineSegment(sketch, "E768", {"start": v(5.79, -8.38) * mm, "end": v(5.79, -8.5) * mm});
            skLineSegment(sketch, "E769", {"start": v(5.79, -8.5) * mm, "end": v(5.91, -8.5) * mm});
            skLineSegment(sketch, "E770", {"start": v(5.91, -8.5) * mm, "end": v(5.91, -8.63) * mm});
            skLineSegment(sketch, "E771", {"start": v(5.91, -8.63) * mm, "end": v(6.04, -8.63) * mm});
            skLineSegment(sketch, "E772", {"start": v(6.04, -8.63) * mm, "end": v(6.04, -8.75) * mm});
            skLineSegment(sketch, "E773", {"start": v(6.04, -8.75) * mm, "end": v(6.29, -8.88) * mm});
            skLineSegment(sketch, "E774", {"start": v(6.29, -8.88) * mm, "end": v(6.29, -9.13) * mm});
            skLineSegment(sketch, "E775", {"start": v(6.29, -9.13) * mm, "end": v(6.16, -9.25) * mm});
            skLineSegment(sketch, "E776", {"start": v(6.16, -9.25) * mm, "end": v(5.79, -9.38) * mm});
            skLineSegment(sketch, "E777", {"start": v(5.79, -9.38) * mm, "end": v(5.66, -9.62) * mm});
            skLineSegment(sketch, "E778", {"start": v(5.66, -9.62) * mm, "end": v(5.41, -9.62) * mm});
            skLineSegment(sketch, "E779", {"start": v(5.41, -9.62) * mm, "end": v(5.41, -9.75) * mm});
            skLineSegment(sketch, "E780", {"start": v(5.41, -9.75) * mm, "end": v(5.17, -9.75) * mm});
            skLineSegment(sketch, "E781", {"start": v(5.17, -9.75) * mm, "end": v(5.17, -9.87) * mm});
            skLineSegment(sketch, "E782", {"start": v(5.17, -9.87) * mm, "end": v(4.92, -9.87) * mm});
            skLineSegment(sketch, "E783", {"start": v(4.92, -9.87) * mm, "end": v(4.92, -10) * mm});
            skLineSegment(sketch, "E784", {"start": v(4.92, -10) * mm, "end": v(4.67, -10) * mm});
            skLineSegment(sketch, "E785", {"start": v(4.67, -10) * mm, "end": v(4.67, -10.12) * mm});
            skLineSegment(sketch, "E786", {"start": v(4.67, -10.12) * mm, "end": v(4.42, -10.12) * mm});
            skLineSegment(sketch, "E787", {"start": v(4.42, -10.12) * mm, "end": v(4.42, -10.25) * mm});
            skLineSegment(sketch, "E788", {"start": v(4.42, -10.25) * mm, "end": v(4.17, -10.25) * mm});
            skLineSegment(sketch, "E789", {"start": v(4.17, -10.25) * mm, "end": v(4.17, -10.37) * mm});
            skLineSegment(sketch, "E790", {"start": v(4.17, -10.37) * mm, "end": v(3.92, -10.5) * mm});
            skLineSegment(sketch, "E791", {"start": v(3.92, -10.5) * mm, "end": v(3.55, -10.62) * mm});
            skLineSegment(sketch, "E792", {"start": v(3.55, -10.62) * mm, "end": v(3.17, -10.62) * mm});
            skLineSegment(sketch, "E793", {"start": v(3.17, -10.62) * mm, "end": v(3.17, -10.75) * mm});
            skLineSegment(sketch, "E794", {"start": v(3.17, -10.75) * mm, "end": v(2.8, -10.75) * mm});
            skLineSegment(sketch, "E795", {"start": v(2.8, -10.75) * mm, "end": v(2.8, -10.87) * mm});
            skLineSegment(sketch, "E796", {"start": v(2.8, -10.87) * mm, "end": v(2.3, -10.87) * mm});
            skLineSegment(sketch, "E797", {"start": v(2.3, -10.87) * mm, "end": v(2.3, -11) * mm});
            skLineSegment(sketch, "E798", {"start": v(2.3, -11) * mm, "end": v(1.43, -11) * mm});
            skLineSegment(sketch, "E799", {"start": v(1.43, -11) * mm, "end": v(1.43, -11.12) * mm});
            skLineSegment(sketch, "E800", {"start": v(1.43, -11.12) * mm, "end": v(1.06, -11.12) * mm});
            skLineSegment(sketch, "E801", {"start": v(1.06, -11.12) * mm, "end": v(0.56, -11.12) * mm});
            skLineSegment(sketch, "E802", {"start": v(0.56, -11.12) * mm, "end": v(0.44, -11.12) * mm});
            skLineSegment(sketch, "E803", {"start": v(0.44, -11.12) * mm, "end": v(0.31, -11.12) * mm});
            skLineSegment(sketch, "E804", {"start": v(0.31, -11.12) * mm, "end": v(0.19, -11.12) * mm});
            skLineSegment(sketch, "E805", {"start": v(0.19, -11.12) * mm, "end": v(0.06, -11.12) * mm});
            skLineSegment(sketch, "E806", {"start": v(0.06, -11.12) * mm, "end": v(-0.06, -11.12) * mm});
            skLineSegment(sketch, "E807", {"start": v(-0.06, -11.12) * mm, "end": v(-0.19, -11.12) * mm});
            skLineSegment(sketch, "E808", {"start": v(-0.19, -11.12) * mm, "end": v(-0.31, -11.12) * mm});
            skLineSegment(sketch, "E809", {"start": v(-0.31, -11.12) * mm, "end": v(-0.44, -11.12) * mm});
            skLineSegment(sketch, "E810", {"start": v(-0.44, -11.12) * mm, "end": v(-0.56, -11.12) * mm});
            skLineSegment(sketch, "E811", {"start": v(-0.56, -11.12) * mm, "end": v(-0.68, -11.12) * mm});
            skLineSegment(sketch, "E812", {"start": v(-0.68, -11.12) * mm, "end": v(-0.8, -11.12) * mm});
            skLineSegment(sketch, "E813", {"start": v(-0.8, -11.12) * mm, "end": v(-1.56, -11.12) * mm});
            skLineSegment(sketch, "E814", {"start": v(-1.56, -11.12) * mm, "end": v(-1.56, -11) * mm});
            skLineSegment(sketch, "E815", {"start": v(-1.56, -11) * mm, "end": v(-2.3, -11) * mm});
            skLineSegment(sketch, "E816", {"start": v(-2.3, -11) * mm, "end": v(-2.3, -10.87) * mm});
            skLineSegment(sketch, "E817", {"start": v(-2.3, -10.87) * mm, "end": v(-2.8, -10.87) * mm});
            skLineSegment(sketch, "E818", {"start": v(-2.8, -10.87) * mm, "end": v(-3.17, -10.75) * mm});
            skLineSegment(sketch, "E819", {"start": v(-3.17, -10.75) * mm, "end": v(-3.17, -10.62) * mm});
            skLineSegment(sketch, "E820", {"start": v(-3.17, -10.62) * mm, "end": v(-3.55, -10.62) * mm});
            skLineSegment(sketch, "E821", {"start": v(-3.55, -10.62) * mm, "end": v(-3.55, -10.5) * mm});
            skLineSegment(sketch, "E822", {"start": v(-3.55, -10.5) * mm, "end": v(-3.92, -10.5) * mm});
            skLineSegment(sketch, "E823", {"start": v(-3.92, -10.5) * mm, "end": v(-4.17, -10.25) * mm});
            skLineSegment(sketch, "E824", {"start": v(-4.17, -10.25) * mm, "end": v(-4.54, -10.25) * mm});
            skLineSegment(sketch, "E825", {"start": v(-4.54, -10.25) * mm, "end": v(-5.04, -10) * mm});
            skLineSegment(sketch, "E826", {"start": v(-5.04, -10) * mm, "end": v(-5.17, -9.75) * mm});
            skLineSegment(sketch, "E827", {"start": v(-5.17, -9.75) * mm, "end": v(-5.66, -9.62) * mm});
            skLineSegment(sketch, "E828", {"start": v(-5.66, -9.62) * mm, "end": v(-5.79, -9.38) * mm});
            skLineSegment(sketch, "E829", {"start": v(-5.79, -9.38) * mm, "end": v(-6.29, -9.13) * mm});
            skLineSegment(sketch, "E830", {"start": v(-6.29, -9.13) * mm, "end": v(-6.29, -8.88) * mm});
            skLineSegment(sketch, "E831", {"start": v(-6.29, -8.88) * mm, "end": v(-6.16, -8.75) * mm});
            skLineSegment(sketch, "E832", {"start": v(-6.16, -8.75) * mm, "end": v(-5.91, -8.5) * mm});
            skLineSegment(sketch, "E833", {"start": v(-5.91, -8.5) * mm, "end": v(-5.79, -8.5) * mm});
            skLineSegment(sketch, "E834", {"start": v(-5.79, -8.5) * mm, "end": v(-5.79, -8.38) * mm});
            skLineSegment(sketch, "E835", {"start": v(-5.79, -8.38) * mm, "end": v(-5.66, -8.38) * mm});
            skLineSegment(sketch, "E836", {"start": v(-5.66, -8.38) * mm, "end": v(-5.54, -8.13) * mm});
            skLineSegment(sketch, "E837", {"start": v(-5.54, -8.13) * mm, "end": v(-5.3, -8.13) * mm});
            skLineSegment(sketch, "E838", {"start": v(-5.3, -8.13) * mm, "end": v(-5.17, -8) * mm});
            skLineSegment(sketch, "E839", {"start": v(-5.17, -8) * mm, "end": v(-4.92, -7.76) * mm});
            skLineSegment(sketch, "E840", {"start": v(-4.92, -7.76) * mm, "end": v(-4.92, -7.63) * mm});
            skLineSegment(sketch, "E841", {"start": v(-4.92, -7.63) * mm, "end": v(-4.8, -7.63) * mm});
            skLineSegment(sketch, "E842", {"start": v(-4.8, -7.63) * mm, "end": v(-4.8, -7.5) * mm});
            skLineSegment(sketch, "E843", {"start": v(-4.8, -7.5) * mm, "end": v(-4.67, -7.5) * mm});
            skLineSegment(sketch, "E844", {"start": v(-4.67, -7.5) * mm, "end": v(-4.67, -7.38) * mm});
            skLineSegment(sketch, "E845", {"start": v(-4.67, -7.38) * mm, "end": v(-4.54, -7.38) * mm});
            skLineSegment(sketch, "E846", {"start": v(-4.54, -7.38) * mm, "end": v(-4.54, -7.26) * mm});
            skLineSegment(sketch, "E847", {"start": v(-4.54, -7.26) * mm, "end": v(-4.42, -7.26) * mm});
            skLineSegment(sketch, "E848", {"start": v(-4.42, -7.26) * mm, "end": v(-4.42, -7.14) * mm});
            skLineSegment(sketch, "E849", {"start": v(-4.42, -7.14) * mm, "end": v(-4.3, -7.14) * mm});
            skLineSegment(sketch, "E850", {"start": v(-4.3, -7.14) * mm, "end": v(-4.3, -7.01) * mm});
            skLineSegment(sketch, "E851", {"start": v(-4.3, -7.01) * mm, "end": v(-4.17, -7.01) * mm});
            skLineSegment(sketch, "E852", {"start": v(-4.17, -7.01) * mm, "end": v(-4.17, -6.89) * mm});
            skLineSegment(sketch, "E853", {"start": v(-4.17, -6.89) * mm, "end": v(-4.05, -6.89) * mm});
            skLineSegment(sketch, "E854", {"start": v(-4.05, -6.89) * mm, "end": v(-4.05, -6.76) * mm});
            skLineSegment(sketch, "E855", {"start": v(-4.05, -6.76) * mm, "end": v(-3.92, -6.76) * mm});
            skLineSegment(sketch, "E856", {"start": v(-3.92, -6.76) * mm, "end": v(-3.92, -6.64) * mm});
            skLineSegment(sketch, "E857", {"start": v(-3.92, -6.64) * mm, "end": v(-3.8, -6.64) * mm});
            skLineSegment(sketch, "E858", {"start": v(-3.8, -6.64) * mm, "end": v(-3.8, -6.51) * mm});
            skLineSegment(sketch, "E859", {"start": v(-3.8, -6.51) * mm, "end": v(-3.67, -6.51) * mm});
            skLineSegment(sketch, "E860", {"start": v(-3.67, -6.51) * mm, "end": v(-3.67, -6.39) * mm});
            skLineSegment(sketch, "E861", {"start": v(-3.67, -6.39) * mm, "end": v(-3.55, -6.39) * mm});
            skLineSegment(sketch, "E862", {"start": v(-3.55, -6.39) * mm, "end": v(-3.55, -6.26) * mm});
            skLineSegment(sketch, "E863", {"start": v(-3.55, -6.26) * mm, "end": v(-3.42, -6.26) * mm});
            skLineSegment(sketch, "E864", {"start": v(-3.42, -6.26) * mm, "end": v(-3.42, -6.14) * mm});
            skLineSegment(sketch, "E865", {"start": v(-3.42, -6.14) * mm, "end": v(-3.3, -6.14) * mm});
            skLineSegment(sketch, "E866", {"start": v(-3.3, -6.14) * mm, "end": v(-3.3, -6.01) * mm});
            skLineSegment(sketch, "E867", {"start": v(-3.3, -6.01) * mm, "end": v(-3.17, -6.01) * mm});
            skLineSegment(sketch, "E868", {"start": v(-3.17, -6.01) * mm, "end": v(-3.17, -5.9) * mm});
            skLineSegment(sketch, "E869", {"start": v(-3.17, -5.9) * mm, "end": v(-3.05, -5.9) * mm});
            skLineSegment(sketch, "E870", {"start": v(-3.05, -5.9) * mm, "end": v(-3.05, -5.77) * mm});
            skLineSegment(sketch, "E871", {"start": v(-3.05, -5.77) * mm, "end": v(-2.93, -5.77) * mm});
            skLineSegment(sketch, "E872", {"start": v(-2.93, -5.77) * mm, "end": v(-2.93, -5.64) * mm});
            skLineSegment(sketch, "E873", {"start": v(-2.93, -5.64) * mm, "end": v(-2.8, -5.64) * mm});
            skLineSegment(sketch, "E874", {"start": v(-2.8, -5.64) * mm, "end": v(-2.8, -5.52) * mm});
            skLineSegment(sketch, "E875", {"start": v(-2.8, -5.52) * mm, "end": v(-2.68, -5.52) * mm});
            skLineSegment(sketch, "E876", {"start": v(-2.68, -5.52) * mm, "end": v(-2.68, -5.4) * mm});
            skLineSegment(sketch, "E877", {"start": v(-2.68, -5.4) * mm, "end": v(-2.55, -5.4) * mm});
            skLineSegment(sketch, "E878", {"start": v(-2.55, -5.4) * mm, "end": v(-2.55, -5.27) * mm});
            skLineSegment(sketch, "E879", {"start": v(-2.55, -5.27) * mm, "end": v(-2.43, -5.27) * mm});
            skLineSegment(sketch, "E880", {"start": v(-2.43, -5.27) * mm, "end": v(-2.43, -5.14) * mm});
            skLineSegment(sketch, "E881", {"start": v(-2.43, -5.14) * mm, "end": v(-2.3, -5.14) * mm});
            skLineSegment(sketch, "E882", {"start": v(-2.3, -5.14) * mm, "end": v(-2.3, -5.02) * mm});
            skLineSegment(sketch, "E883", {"start": v(-2.3, -5.02) * mm, "end": v(-1.93, -4.65) * mm});
            skLineSegment(sketch, "E884", {"start": v(-1.93, -4.65) * mm, "end": v(-1.68, -4.65) * mm});
            skLineSegment(sketch, "E885", {"start": v(-1.68, -4.65) * mm, "end": v(-1.56, -4.52) * mm});
            skLineSegment(sketch, "E886", {"start": v(-1.56, -4.52) * mm, "end": v(-1.3, -4.27) * mm});
            skLineSegment(sketch, "E887", {"start": v(-1.3, -4.27) * mm, "end": v(-1.3, -4.15) * mm});
            skLineSegment(sketch, "E888", {"start": v(-1.3, -4.15) * mm, "end": v(-1.18, -4.15) * mm});
            skLineSegment(sketch, "E889", {"start": v(-1.18, -4.15) * mm, "end": v(-1.18, -4.02) * mm});
            skLineSegment(sketch, "E890", {"start": v(-1.18, -4.02) * mm, "end": v(-1.06, -4.02) * mm});
            skLineSegment(sketch, "E891", {"start": v(-1.06, -4.02) * mm, "end": v(-1.06, -3.9) * mm});
            skLineSegment(sketch, "E892", {"start": v(-1.06, -3.9) * mm, "end": v(-0.93, -3.9) * mm});
            skLineSegment(sketch, "E893", {"start": v(-0.93, -3.9) * mm, "end": v(-0.93, -3.77) * mm});
            skLineSegment(sketch, "E894", {"start": v(-0.93, -3.77) * mm, "end": v(-0.56, -3.53) * mm});
            skLineSegment(sketch, "E895", {"start": v(-0.56, -3.53) * mm, "end": v(-0.56, -3.03) * mm});
            skLineSegment(sketch, "E896", {"start": v(-0.56, -3.03) * mm, "end": v(-0.56, -2.9) * mm});
            skLineSegment(sketch, "E897", {"start": v(-0.56, -2.9) * mm, "end": v(-0.56, -2.78) * mm});
            skLineSegment(sketch, "E898", {"start": v(-0.56, -2.78) * mm, "end": v(-0.56, -2.65) * mm});
            skLineSegment(sketch, "E899", {"start": v(-0.56, -2.65) * mm, "end": v(-0.56, -2.53) * mm});
            skLineSegment(sketch, "E900", {"start": v(-0.56, -2.53) * mm, "end": v(-0.56, -2.4) * mm});
            skLineSegment(sketch, "E901", {"start": v(-0.56, -2.4) * mm, "end": v(-0.56, -2.28) * mm});
            skLineSegment(sketch, "E902", {"start": v(-0.56, -2.28) * mm, "end": v(-0.56, -2.16) * mm});
            skLineSegment(sketch, "E903", {"start": v(-0.56, -2.16) * mm, "end": v(-0.56, -2.03) * mm});
            skLineSegment(sketch, "E904", {"start": v(-0.56, -2.03) * mm, "end": v(-0.56, -1.9) * mm});
            skLineSegment(sketch, "E905", {"start": v(-0.56, -1.9) * mm, "end": v(-0.56, -1.78) * mm});
            skLineSegment(sketch, "E906", {"start": v(-0.56, -1.78) * mm, "end": v(-0.56, -1.66) * mm});
            skLineSegment(sketch, "E907", {"start": v(-0.56, -1.66) * mm, "end": v(-0.56, -1.53) * mm});
            skLineSegment(sketch, "E908", {"start": v(-0.56, -1.53) * mm, "end": v(-0.56, -1.4) * mm});
            skLineSegment(sketch, "E909", {"start": v(-0.56, -1.4) * mm, "end": v(-0.56, -1.28) * mm});
            skLineSegment(sketch, "E910", {"start": v(-0.56, -1.28) * mm, "end": v(-0.56, -1.16) * mm});
            skLineSegment(sketch, "E911", {"start": v(-0.56, -1.16) * mm, "end": v(-0.56, -1.04) * mm});
            skLineSegment(sketch, "E912", {"start": v(-0.56, -1.04) * mm, "end": v(-0.56, -0.91) * mm});
            skLineSegment(sketch, "E913", {"start": v(-0.56, -0.91) * mm, "end": v(-0.56, -0.79) * mm});
            skLineSegment(sketch, "E914", {"start": v(-0.56, -0.79) * mm, "end": v(-0.56, -0.66) * mm});
            skLineSegment(sketch, "E915", {"start": v(-0.56, -0.66) * mm, "end": v(-0.56, -0.54) * mm});
            skLineSegment(sketch, "E916", {"start": v(-0.56, -0.54) * mm, "end": v(-0.56, -0.41) * mm});
            skLineSegment(sketch, "E917", {"start": v(-0.56, -0.41) * mm, "end": v(-0.56, -0.29) * mm});
            skLineSegment(sketch, "E918", {"start": v(-0.56, -0.29) * mm, "end": v(-0.56, -0.16) * mm});
            skLineSegment(sketch, "E919", {"start": v(-0.56, -0.16) * mm, "end": v(-0.56, -0.04) * mm});
            skLineSegment(sketch, "E920", {"start": v(-0.56, -0.04) * mm, "end": v(-0.56, 0.08) * mm});
            skLineSegment(sketch, "E921", {"start": v(-0.56, 0.08) * mm, "end": v(-0.56, 0.2) * mm});
            skLineSegment(sketch, "E922", {"start": v(-0.56, 0.2) * mm, "end": v(-0.56, 0.33) * mm});
            skLineSegment(sketch, "E923", {"start": v(-0.56, 0.33) * mm, "end": v(-0.56, 0.46) * mm});
            skLineSegment(sketch, "E924", {"start": v(-0.56, 0.46) * mm, "end": v(-0.56, 0.58) * mm});
            skLineSegment(sketch, "E925", {"start": v(-0.56, 0.58) * mm, "end": v(-0.56, 0.7) * mm});
            skLineSegment(sketch, "E926", {"start": v(-0.56, 0.7) * mm, "end": v(-0.56, 0.83) * mm});
            skLineSegment(sketch, "E927", {"start": v(-0.56, 0.83) * mm, "end": v(-0.56, 0.96) * mm});
            skLineSegment(sketch, "E928", {"start": v(-0.56, 0.96) * mm, "end": v(-0.56, 1.08) * mm});
            skLineSegment(sketch, "E929", {"start": v(-0.56, 1.08) * mm, "end": v(-0.56, 1.2) * mm});
            skLineSegment(sketch, "E930", {"start": v(-0.56, 1.2) * mm, "end": v(-0.56, 1.33) * mm});
            skLineSegment(sketch, "E931", {"start": v(-0.56, 1.33) * mm, "end": v(-0.56, 1.45) * mm});
            skLineSegment(sketch, "E932", {"start": v(-0.56, 1.45) * mm, "end": v(-0.56, 1.58) * mm});
            skLineSegment(sketch, "E933", {"start": v(-0.56, 1.58) * mm, "end": v(-0.56, 1.7) * mm});
            skLineSegment(sketch, "E934", {"start": v(-0.56, 1.7) * mm, "end": v(-0.56, 1.83) * mm});
            skLineSegment(sketch, "E935", {"start": v(-0.56, 1.83) * mm, "end": v(-0.56, 1.95) * mm});
            skLineSegment(sketch, "E936", {"start": v(-0.56, 1.95) * mm, "end": v(-0.56, 2.08) * mm});
            skLineSegment(sketch, "E937", {"start": v(-0.56, 2.08) * mm, "end": v(-0.56, 2.2) * mm});
            skLineSegment(sketch, "E938", {"start": v(-0.56, 2.2) * mm, "end": v(-0.56, 2.33) * mm});
            skLineSegment(sketch, "E939", {"start": v(-0.56, 2.33) * mm, "end": v(-0.56, 2.45) * mm});
            skLineSegment(sketch, "E940", {"start": v(-0.56, 2.45) * mm, "end": v(-0.56, 2.57) * mm});
            skLineSegment(sketch, "E941", {"start": v(-0.56, 2.57) * mm, "end": v(-0.56, 2.7) * mm});
            skLineSegment(sketch, "E942", {"start": v(-0.56, 2.7) * mm, "end": v(-0.56, 2.82) * mm});
            skLineSegment(sketch, "E943", {"start": v(-0.56, 2.82) * mm, "end": v(-0.56, 2.95) * mm});
            skLineSegment(sketch, "E944", {"start": v(-0.56, 2.95) * mm, "end": v(-0.56, 3.07) * mm});
            skLineSegment(sketch, "E945", {"start": v(-0.56, 3.07) * mm, "end": v(-0.56, 3.2) * mm});
            skLineSegment(sketch, "E946", {"start": v(-0.56, 3.2) * mm, "end": v(-0.56, 3.32) * mm});
            skLineSegment(sketch, "E947", {"start": v(-0.56, 3.32) * mm, "end": v(-0.56, 3.45) * mm});
            skLineSegment(sketch, "E948", {"start": v(-0.56, 3.45) * mm, "end": v(-0.56, 3.57) * mm});
            skLineSegment(sketch, "E949", {"start": v(-0.56, 3.57) * mm, "end": v(-0.56, 3.7) * mm});
            skLineSegment(sketch, "E950", {"start": v(-0.56, 3.7) * mm, "end": v(-0.56, 3.82) * mm});
            skLineSegment(sketch, "E951", {"start": v(-0.56, 3.82) * mm, "end": v(-0.56, 3.94) * mm});
            skLineSegment(sketch, "E952", {"start": v(-0.56, 3.94) * mm, "end": v(-0.56, 4.07) * mm});
            skLineSegment(sketch, "E953", {"start": v(-0.56, 4.07) * mm, "end": v(-0.56, 4.2) * mm});
            skLineSegment(sketch, "E954", {"start": v(-0.56, 4.2) * mm, "end": v(-0.56, 4.32) * mm});
            skLineSegment(sketch, "E955", {"start": v(-0.56, 4.32) * mm, "end": v(-0.56, 4.44) * mm});
            skLineSegment(sketch, "E956", {"start": v(-0.56, 4.44) * mm, "end": v(-0.56, 4.57) * mm});
            skLineSegment(sketch, "E957", {"start": v(-0.56, 4.57) * mm, "end": v(-0.56, 4.7) * mm});
            skLineSegment(sketch, "E958", {"start": v(-0.56, 4.7) * mm, "end": v(-0.56, 4.81) * mm});
            skLineSegment(sketch, "E959", {"start": v(-0.56, 4.81) * mm, "end": v(-0.56, 4.94) * mm});
            skLineSegment(sketch, "E960", {"start": v(-0.56, 4.94) * mm, "end": v(-0.56, 5.06) * mm});
            skLineSegment(sketch, "E961", {"start": v(-0.56, 5.06) * mm, "end": v(-0.56, 5.19) * mm});
            skLineSegment(sketch, "E962", {"start": v(-0.56, 5.19) * mm, "end": v(-0.56, 5.31) * mm});
            skLineSegment(sketch, "E963", {"start": v(-0.56, 5.31) * mm, "end": v(-0.56, 5.94) * mm});
            skLineSegment(sketch, "E964", {"start": v(-0.56, 5.94) * mm, "end": v(-0.68, 5.94) * mm});
            skLineSegment(sketch, "E965", {"start": v(-0.68, 5.94) * mm, "end": v(-0.8, 5.44) * mm});
            skLineSegment(sketch, "E966", {"start": v(-0.8, 5.44) * mm, "end": v(-1.06, 5.19) * mm});
            skLineSegment(sketch, "E967", {"start": v(-1.06, 5.19) * mm, "end": v(-1.06, 4.94) * mm});
            skLineSegment(sketch, "E968", {"start": v(-1.06, 4.94) * mm, "end": v(-1.18, 4.94) * mm});
            skLineSegment(sketch, "E969", {"start": v(-1.18, 4.94) * mm, "end": v(-1.18, 4.7) * mm});
            skLineSegment(sketch, "E970", {"start": v(-1.18, 4.7) * mm, "end": v(-1.3, 4.7) * mm});
            skLineSegment(sketch, "E971", {"start": v(-1.3, 4.7) * mm, "end": v(-1.3, 4.44) * mm});
            skLineSegment(sketch, "E972", {"start": v(-1.3, 4.44) * mm, "end": v(-1.43, 4.44) * mm});
            skLineSegment(sketch, "E973", {"start": v(-1.43, 4.44) * mm, "end": v(-1.43, 4.2) * mm});
            skLineSegment(sketch, "E974", {"start": v(-1.43, 4.2) * mm, "end": v(-1.56, 4.2) * mm});
            skLineSegment(sketch, "E975", {"start": v(-1.56, 4.2) * mm, "end": v(-1.68, 3.94) * mm});
            skLineSegment(sketch, "E976", {"start": v(-1.68, 3.94) * mm, "end": v(-1.68, 3.57) * mm});
            skLineSegment(sketch, "E977", {"start": v(-1.68, 3.57) * mm, "end": v(-1.8, 3.32) * mm});
            skLineSegment(sketch, "E978", {"start": v(-1.8, 3.32) * mm, "end": v(-1.93, 3.32) * mm});
            skLineSegment(sketch, "E979", {"start": v(-1.93, 3.32) * mm, "end": v(-1.93, 3.07) * mm});
            skLineSegment(sketch, "E980", {"start": v(-1.93, 3.07) * mm, "end": v(-2.05, 3.07) * mm});
            skLineSegment(sketch, "E981", {"start": v(-2.05, 3.07) * mm, "end": v(-2.05, 2.82) * mm});
            skLineSegment(sketch, "E982", {"start": v(-2.05, 2.82) * mm, "end": v(-2.18, 2.82) * mm});
            skLineSegment(sketch, "E983", {"start": v(-2.18, 2.82) * mm, "end": v(-2.18, 2.57) * mm});
            skLineSegment(sketch, "E984", {"start": v(-2.18, 2.57) * mm, "end": v(-2.3, 2.57) * mm});
            skLineSegment(sketch, "E985", {"start": v(-2.3, 2.57) * mm, "end": v(-2.3, 2.33) * mm});
            skLineSegment(sketch, "E986", {"start": v(-2.3, 2.33) * mm, "end": v(-2.55, 2.08) * mm});
            skLineSegment(sketch, "E987", {"start": v(-2.55, 2.08) * mm, "end": v(-2.55, 1.7) * mm});
            skLineSegment(sketch, "E988", {"start": v(-2.55, 1.7) * mm, "end": v(-2.68, 1.45) * mm});
            skLineSegment(sketch, "E989", {"start": v(-2.68, 1.45) * mm, "end": v(-2.8, 1.45) * mm});
            skLineSegment(sketch, "E990", {"start": v(-2.8, 1.45) * mm, "end": v(-2.8, 1.2) * mm});
            skLineSegment(sketch, "E991", {"start": v(-2.8, 1.2) * mm, "end": v(-2.93, 1.2) * mm});
            skLineSegment(sketch, "E992", {"start": v(-2.93, 1.2) * mm, "end": v(-2.93, 0.96) * mm});
            skLineSegment(sketch, "E993", {"start": v(-2.93, 0.96) * mm, "end": v(-3.05, 0.96) * mm});
            skLineSegment(sketch, "E994", {"start": v(-3.05, 0.96) * mm, "end": v(-3.05, 0.7) * mm});
            skLineSegment(sketch, "E995", {"start": v(-3.05, 0.7) * mm, "end": v(-3.17, 0.7) * mm});
            skLineSegment(sketch, "E996", {"start": v(-3.17, 0.7) * mm, "end": v(-3.3, 0.46) * mm});
            skLineSegment(sketch, "E997", {"start": v(-3.3, 0.46) * mm, "end": v(-3.3, 0.08) * mm});
            skLineSegment(sketch, "E998", {"start": v(-3.3, 0.08) * mm, "end": v(-3.42, -0.16) * mm});
            skLineSegment(sketch, "E999", {"start": v(-3.42, -0.16) * mm, "end": v(-3.67, -0.41) * mm});
            skLineSegment(sketch, "E1000", {"start": v(-3.67, -0.41) * mm, "end": v(-3.8, -0.41) * mm});
            skLineSegment(sketch, "E1001", {"start": v(-3.8, -0.41) * mm, "end": v(-3.8, -0.54) * mm});
            skLineSegment(sketch, "E1002", {"start": v(-3.8, -0.54) * mm, "end": v(-3.92, -0.54) * mm});
            skLineSegment(sketch, "E1003", {"start": v(-3.92, -0.54) * mm, "end": v(-3.92, -0.66) * mm});
            skLineSegment(sketch, "E1004", {"start": v(-3.92, -0.66) * mm, "end": v(-4.05, -0.66) * mm});
            skLineSegment(sketch, "E1005", {"start": v(-4.05, -0.66) * mm, "end": v(-4.05, -0.79) * mm});
            skLineSegment(sketch, "E1006", {"start": v(-4.05, -0.79) * mm, "end": v(-4.17, -0.79) * mm});
            skLineSegment(sketch, "E1007", {"start": v(-4.17, -0.79) * mm, "end": v(-4.17, -0.91) * mm});
            skLineSegment(sketch, "E1008", {"start": v(-4.17, -0.91) * mm, "end": v(-4.3, -0.91) * mm});
            skLineSegment(sketch, "E1009", {"start": v(-4.3, -0.91) * mm, "end": v(-4.3, -1.04) * mm});
            skLineSegment(sketch, "E1010", {"start": v(-4.3, -1.04) * mm, "end": v(-4.42, -1.04) * mm});
            skLineSegment(sketch, "E1011", {"start": v(-4.42, -1.04) * mm, "end": v(-4.42, -1.16) * mm});
            skLineSegment(sketch, "E1012", {"start": v(-4.42, -1.16) * mm, "end": v(-4.54, -1.16) * mm});
            skLineSegment(sketch, "E1013", {"start": v(-4.54, -1.16) * mm, "end": v(-4.54, -1.28) * mm});
            skLineSegment(sketch, "E1014", {"start": v(-4.54, -1.28) * mm, "end": v(-4.67, -1.28) * mm});
            skLineSegment(sketch, "E1015", {"start": v(-4.67, -1.28) * mm, "end": v(-4.8, -1.53) * mm});
            skLineSegment(sketch, "E1016", {"start": v(-4.8, -1.53) * mm, "end": v(-5.04, -1.53) * mm});
            skLineSegment(sketch, "E1017", {"start": v(-5.04, -1.53) * mm, "end": v(-5.17, -1.66) * mm});
            skLineSegment(sketch, "E1018", {"start": v(-5.17, -1.66) * mm, "end": v(-5.41, -1.9) * mm});
            skLineSegment(sketch, "E1019", {"start": v(-5.41, -1.9) * mm, "end": v(-5.41, -2.03) * mm});
            skLineSegment(sketch, "E1020", {"start": v(-5.41, -2.03) * mm, "end": v(-5.54, -2.03) * mm});
            skLineSegment(sketch, "E1021", {"start": v(-5.54, -2.03) * mm, "end": v(-5.54, -2.16) * mm});
            skLineSegment(sketch, "E1022", {"start": v(-5.54, -2.16) * mm, "end": v(-5.66, -2.16) * mm});
            skLineSegment(sketch, "E1023", {"start": v(-5.66, -2.16) * mm, "end": v(-5.66, -2.28) * mm});
            skLineSegment(sketch, "E1024", {"start": v(-5.66, -2.28) * mm, "end": v(-5.79, -2.28) * mm});
            skLineSegment(sketch, "E1025", {"start": v(-5.79, -2.28) * mm, "end": v(-5.79, -2.4) * mm});
            skLineSegment(sketch, "E1026", {"start": v(-5.79, -2.4) * mm, "end": v(-5.91, -2.4) * mm});
            skLineSegment(sketch, "E1027", {"start": v(-5.91, -2.4) * mm, "end": v(-5.91, -2.53) * mm});
            skLineSegment(sketch, "E1028", {"start": v(-5.91, -2.53) * mm, "end": v(-6.04, -2.53) * mm});
            skLineSegment(sketch, "E1029", {"start": v(-6.04, -2.53) * mm, "end": v(-6.04, -2.65) * mm});
            skLineSegment(sketch, "E1030", {"start": v(-6.04, -2.65) * mm, "end": v(-6.16, -2.65) * mm});
            skLineSegment(sketch, "E1031", {"start": v(-6.16, -2.65) * mm, "end": v(-6.16, -2.78) * mm});
            skLineSegment(sketch, "E1032", {"start": v(-6.16, -2.78) * mm, "end": v(-6.29, -2.78) * mm});
            skLineSegment(sketch, "E1033", {"start": v(-6.29, -2.78) * mm, "end": v(-6.29, -2.9) * mm});
            skLineSegment(sketch, "E1034", {"start": v(-6.29, -2.9) * mm, "end": v(-6.41, -2.9) * mm});
            skLineSegment(sketch, "E1035", {"start": v(-6.41, -2.9) * mm, "end": v(-6.41, -3.03) * mm});
            skLineSegment(sketch, "E1036", {"start": v(-6.41, -3.03) * mm, "end": v(-6.54, -3.03) * mm});
            skLineSegment(sketch, "E1037", {"start": v(-6.54, -3.03) * mm, "end": v(-6.54, -3.15) * mm});
            skLineSegment(sketch, "E1038", {"start": v(-6.54, -3.15) * mm, "end": v(-6.66, -3.15) * mm});
            skLineSegment(sketch, "E1039", {"start": v(-6.66, -3.15) * mm, "end": v(-6.66, -3.28) * mm});
            skLineSegment(sketch, "E1040", {"start": v(-6.66, -3.28) * mm, "end": v(-6.78, -3.28) * mm});
            skLineSegment(sketch, "E1041", {"start": v(-6.78, -3.28) * mm, "end": v(-6.78, -3.4) * mm});
            skLineSegment(sketch, "E1042", {"start": v(-6.78, -3.4) * mm, "end": v(-6.9, -3.4) * mm});
            skLineSegment(sketch, "E1043", {"start": v(-6.9, -3.4) * mm, "end": v(-6.9, -3.53) * mm});
            skLineSegment(sketch, "E1044", {"start": v(-6.9, -3.53) * mm, "end": v(-7.03, -3.53) * mm});
            skLineSegment(sketch, "E1045", {"start": v(-7.03, -3.53) * mm, "end": v(-7.03, -3.65) * mm});
            skLineSegment(sketch, "E1046", {"start": v(-7.03, -3.65) * mm, "end": v(-7.16, -3.65) * mm});
            skLineSegment(sketch, "E1047", {"start": v(-7.16, -3.65) * mm, "end": v(-7.16, -3.77) * mm});
            skLineSegment(sketch, "E1048", {"start": v(-7.16, -3.77) * mm, "end": v(-7.28, -3.77) * mm});
            skLineSegment(sketch, "E1049", {"start": v(-7.28, -3.77) * mm, "end": v(-7.28, -3.9) * mm});
            skLineSegment(sketch, "E1050", {"start": v(-7.28, -3.9) * mm, "end": v(-7.4, -3.9) * mm});
            skLineSegment(sketch, "E1051", {"start": v(-7.4, -3.9) * mm, "end": v(-7.4, -4.02) * mm});
            skLineSegment(sketch, "E1052", {"start": v(-7.4, -4.02) * mm, "end": v(-7.53, -4.02) * mm});
            skLineSegment(sketch, "E1053", {"start": v(-7.53, -4.02) * mm, "end": v(-7.53, -4.15) * mm});
            skLineSegment(sketch, "E1054", {"start": v(-7.53, -4.15) * mm, "end": v(-7.66, -4.15) * mm});
            skLineSegment(sketch, "E1055", {"start": v(-7.66, -4.15) * mm, "end": v(-7.66, -4.27) * mm});
            skLineSegment(sketch, "E1056", {"start": v(-7.66, -4.27) * mm, "end": v(-7.78, -4.27) * mm});
            skLineSegment(sketch, "E1057", {"start": v(-7.78, -4.27) * mm, "end": v(-7.78, -4.4) * mm});
            skLineSegment(sketch, "E1058", {"start": v(-7.78, -4.4) * mm, "end": v(-7.9, -4.4) * mm});
            skLineSegment(sketch, "E1059", {"start": v(-7.9, -4.4) * mm, "end": v(-7.9, -4.52) * mm});
            skLineSegment(sketch, "E1060", {"start": v(-7.9, -4.52) * mm, "end": v(-8.03, -4.52) * mm});
            skLineSegment(sketch, "E1061", {"start": v(-8.03, -4.52) * mm, "end": v(-8.03, -4.65) * mm});
            skLineSegment(sketch, "E1062", {"start": v(-8.03, -4.65) * mm, "end": v(-8.15, -4.65) * mm});
            skLineSegment(sketch, "E1063", {"start": v(-8.15, -4.65) * mm, "end": v(-8.15, -4.77) * mm});
            skLineSegment(sketch, "E1064", {"start": v(-8.15, -4.77) * mm, "end": v(-8.28, -4.77) * mm});
            skLineSegment(sketch, "E1065", {"start": v(-8.28, -4.77) * mm, "end": v(-8.28, -4.9) * mm});
            skLineSegment(sketch, "E1066", {"start": v(-8.28, -4.9) * mm, "end": v(-8.53, -5.14) * mm});
            skLineSegment(sketch, "E1067", {"start": v(-8.53, -5.14) * mm, "end": v(-8.78, -5.14) * mm});
            skLineSegment(sketch, "E1068", {"start": v(-8.78, -5.14) * mm, "end": v(-8.9, -5.27) * mm});
            skLineSegment(sketch, "E1069", {"start": v(-8.9, -5.27) * mm, "end": v(-9.02, -5.52) * mm});
            skLineSegment(sketch, "E1070", {"start": v(-9.02, -5.52) * mm, "end": v(-9.4, -5.64) * mm});
            skLineSegment(sketch, "E1071", {"start": v(-9.4, -5.64) * mm, "end": v(-9.52, -5.14) * mm});
            skLineSegment(sketch, "E1072", {"start": v(-9.52, -5.14) * mm, "end": v(-9.65, -5.14) * mm});
            skLineSegment(sketch, "E1073", {"start": v(-9.65, -5.14) * mm, "end": v(-9.65, -4.9) * mm});
            skLineSegment(sketch, "E1074", {"start": v(-9.65, -4.9) * mm, "end": v(-9.9, -4.65) * mm});
            skLineSegment(sketch, "E1075", {"start": v(-9.9, -4.65) * mm, "end": v(-10.02, -4.27) * mm});
            skLineSegment(sketch, "E1076", {"start": v(-10.02, -4.27) * mm, "end": v(-10.02, -3.77) * mm});
            skLineSegment(sketch, "E1077", {"start": v(-10.02, -3.77) * mm, "end": v(-10.27, -3.53) * mm});
            skLineSegment(sketch, "E1078", {"start": v(-10.27, -3.53) * mm, "end": v(-10.27, -2.9) * mm});
            skLineSegment(sketch, "E1079", {"start": v(-10.27, -2.9) * mm, "end": v(-10.4, -2.9) * mm});
            skLineSegment(sketch, "E1080", {"start": v(-10.4, -2.9) * mm, "end": v(-10.4, -2.28) * mm});
            skLineSegment(sketch, "E1081", {"start": v(-10.4, -2.28) * mm, "end": v(-10.52, -2.28) * mm});
            skLineSegment(sketch, "E1082", {"start": v(-10.52, -2.28) * mm, "end": v(-10.52, -1.9) * mm});
            skLineSegment(sketch, "E1083", {"start": v(-10.52, -1.9) * mm, "end": v(-10.52, -1.04) * mm});
            skLineSegment(sketch, "E1084", {"start": v(-10.52, -1.04) * mm, "end": v(-10.64, -1.04) * mm});
            skLineSegment(sketch, "E1085", {"start": v(-10.64, -1.04) * mm, "end": v(-10.64, -0.29) * mm});
            skLineSegment(sketch, "E1086", {"start": v(-10.64, -0.29) * mm, "end": v(-10.52, -0.29) * mm});
            skLineSegment(sketch, "E1087", {"start": v(-10.52, -0.29) * mm, "end": v(-10.52, 0.08) * mm});
            skLineSegment(sketch, "E1088", {"start": v(-10.52, 0.08) * mm, "end": v(-10.52, 1.08) * mm});
            skLineSegment(sketch, "E1089", {"start": v(-10.52, 1.08) * mm, "end": v(-10.4, 1.08) * mm});
            skLineSegment(sketch, "E1090", {"start": v(-10.4, 1.08) * mm, "end": v(-10.4, 1.83) * mm});
            skLineSegment(sketch, "E1091", {"start": v(-10.4, 1.83) * mm, "end": v(-10.27, 1.83) * mm});
            skLineSegment(sketch, "E1092", {"start": v(-10.27, 1.83) * mm, "end": v(-10.27, 2.33) * mm});
            skLineSegment(sketch, "E1093", {"start": v(-10.27, 2.33) * mm, "end": v(-10.15, 2.7) * mm});
            skLineSegment(sketch, "E1094", {"start": v(-10.15, 2.7) * mm, "end": v(-10.02, 2.7) * mm});
            skLineSegment(sketch, "E1095", {"start": v(-10.02, 2.7) * mm, "end": v(-10.02, 3.07) * mm});
            skLineSegment(sketch, "E1096", {"start": v(-10.02, 3.07) * mm, "end": v(-9.9, 3.07) * mm});
            skLineSegment(sketch, "E1097", {"start": v(-9.9, 3.07) * mm, "end": v(-9.9, 3.45) * mm});
            skLineSegment(sketch, "E1098", {"start": v(-9.9, 3.45) * mm, "end": v(-9.65, 3.7) * mm});
            skLineSegment(sketch, "E1099", {"start": v(-9.65, 3.7) * mm, "end": v(-9.65, 3.94) * mm});
            skLineSegment(sketch, "E1100", {"start": v(-9.65, 3.94) * mm, "end": v(-9.52, 3.94) * mm});
            skLineSegment(sketch, "E1101", {"start": v(-9.52, 3.94) * mm, "end": v(-9.52, 4.2) * mm});
            skLineSegment(sketch, "E1102", {"start": v(-9.52, 4.2) * mm, "end": v(-9.4, 4.2) * mm});
            skLineSegment(sketch, "E1103", {"start": v(-9.4, 4.2) * mm, "end": v(-9.4, 4.44) * mm});
            skLineSegment(sketch, "E1104", {"start": v(-9.4, 4.44) * mm, "end": v(-9.27, 4.44) * mm});
            skLineSegment(sketch, "E1105", {"start": v(-9.27, 4.44) * mm, "end": v(-9.27, 4.7) * mm});
            skLineSegment(sketch, "E1106", {"start": v(-9.27, 4.7) * mm, "end": v(-9.15, 4.7) * mm});
            skLineSegment(sketch, "E1107", {"start": v(-9.15, 4.7) * mm, "end": v(-9.15, 4.94) * mm});
            skLineSegment(sketch, "E1108", {"start": v(-9.15, 4.94) * mm, "end": v(-8.9, 5.06) * mm});
            skLineSegment(sketch, "E1109", {"start": v(-8.9, 5.06) * mm, "end": v(-8.9, 5.31) * mm});
            skLineSegment(sketch, "E1110", {"start": v(-8.9, 5.31) * mm, "end": v(-8.65, 5.44) * mm});
            skLineSegment(sketch, "E1111", {"start": v(-8.65, 5.44) * mm, "end": v(-8.65, 5.69) * mm});
            skLineSegment(sketch, "E1112", {"start": v(-8.65, 5.69) * mm, "end": v(-8.15, 6.06) * mm});
            skLineSegment(sketch, "E1113", {"start": v(-8.15, 6.06) * mm, "end": v(-8.15, 6.3) * mm});
            skLineSegment(sketch, "E1114", {"start": v(-8.15, 6.3) * mm, "end": v(-8.03, 6.43) * mm});
            skLineSegment(sketch, "E1115", {"start": v(-8.03, 6.43) * mm, "end": v(-7.78, 6.68) * mm});
            skLineSegment(sketch, "E1116", {"start": v(-7.78, 6.68) * mm, "end": v(-7.66, 6.68) * mm});
            skLineSegment(sketch, "E1117", {"start": v(-7.66, 6.68) * mm, "end": v(-7.66, 6.8) * mm});
            skLineSegment(sketch, "E1118", {"start": v(-7.66, 6.8) * mm, "end": v(-7.53, 6.8) * mm});
            skLineSegment(sketch, "E1119", {"start": v(-7.53, 6.8) * mm, "end": v(-7.28, 7.06) * mm});
            skLineSegment(sketch, "E1120", {"start": v(-7.28, 7.06) * mm, "end": v(-7.28, 7.18) * mm});
            skLineSegment(sketch, "E1121", {"start": v(-7.28, 7.18) * mm, "end": v(-7.78, 7.55) * mm});
            skLineSegment(sketch, "E1122", {"start": v(-7.78, 7.55) * mm, "end": v(-7.78, 7.8) * mm});
            skLineSegment(sketch, "E1123", {"start": v(-7.78, 7.8) * mm, "end": v(-7.9, 7.93) * mm});
            skLineSegment(sketch, "E1124", {"start": v(-7.9, 7.93) * mm, "end": v(-8.53, 8.42) * mm});
            skLineSegment(sketch, "E1125", {"start": v(-8.53, 8.42) * mm, "end": v(-8.53, 8.67) * mm});
            skLineSegment(sketch, "E1126", {"start": v(-8.53, 8.67) * mm, "end": v(-8.65, 8.8) * mm});
            skLineSegment(sketch, "E1127", {"start": v(-8.65, 8.8) * mm, "end": v(-9.27, 9.3) * mm});
            skLineSegment(sketch, "E1128", {"start": v(-9.27, 9.3) * mm, "end": v(-9.27, 9.55) * mm});
            skLineSegment(sketch, "E1129", {"start": v(-9.27, 9.55) * mm, "end": v(-9.4, 9.67) * mm});
            skLineSegment(sketch, "E1130", {"start": v(-9.4, 9.67) * mm, "end": v(-9.9, 10.04) * mm});
            skLineSegment(sketch, "E1131", {"start": v(-9.9, 10.04) * mm, "end": v(-10.02, 10.17) * mm});
            skLineSegment(sketch, "E1132", {"start": v(-10.02, 10.17) * mm, "end": v(-10.02, 10.42) * mm});
            skLineSegment(sketch, "E1133", {"start": v(-10.02, 10.42) * mm, "end": v(-10.27, 10.42) * mm});
            skSolve(sketch);
        }
        {
            var Q0;
            Q0 = qSketchRegion(id + "F7", true);
            extrude(context, id + "F8", {"entities" : qUnion([Q0]), "operationType" : NewBodyOperationType.REMOVE, "oppositeDirection" : true, "depth" : 1 * mm, "offsetDistance" : 25 * mm});
        }
    });
